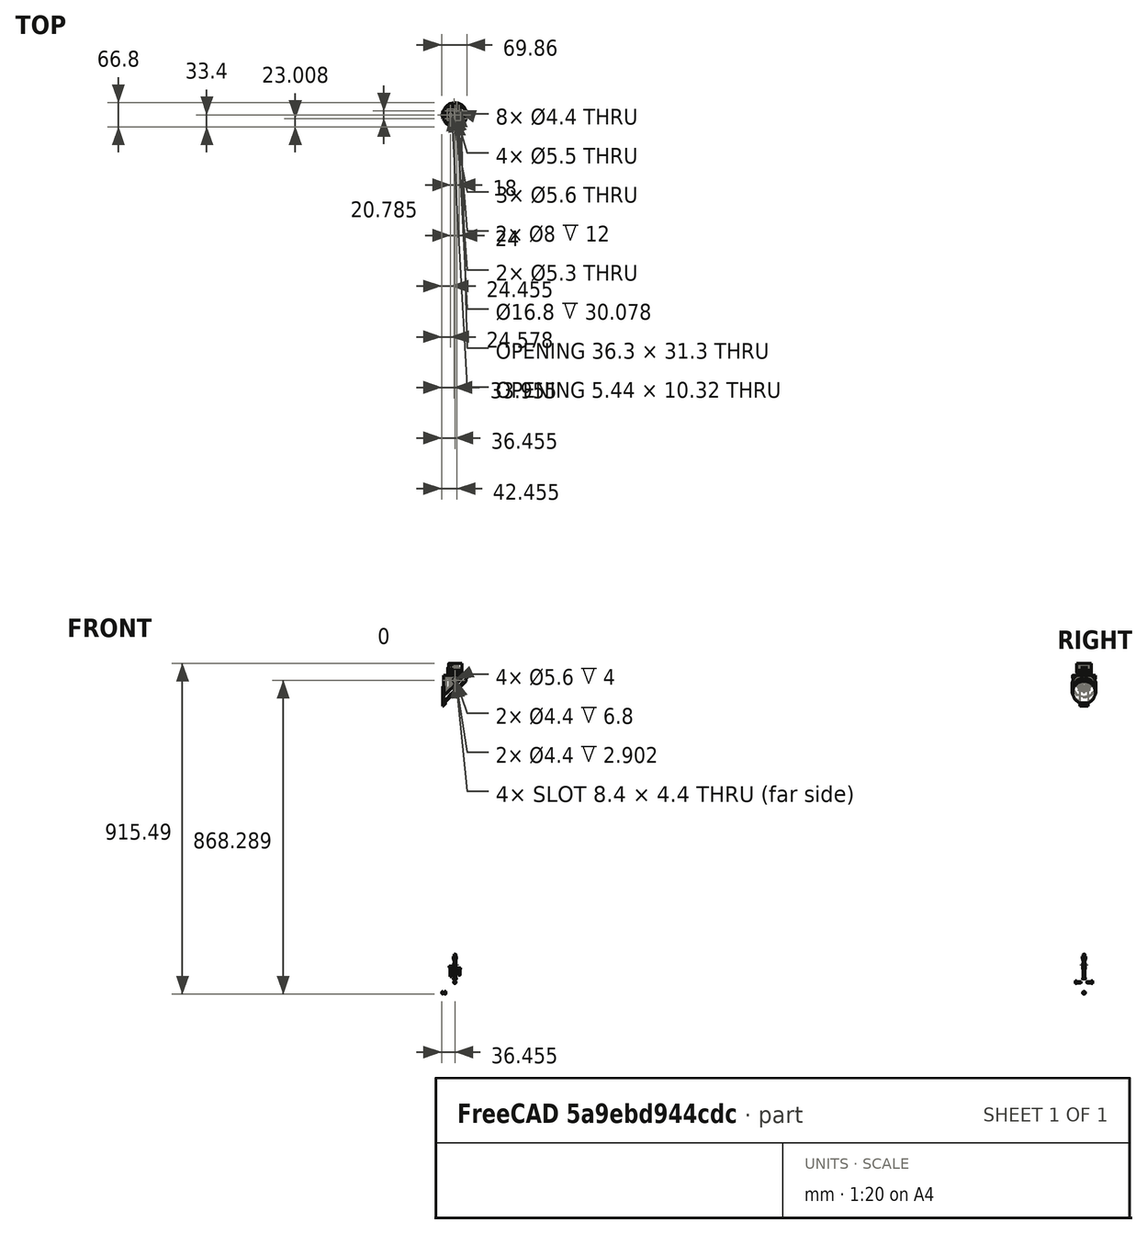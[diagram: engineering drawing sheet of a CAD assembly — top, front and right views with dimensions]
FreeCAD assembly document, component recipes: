
FREECAD ASSEMBLY — COMPONENT RECIPES ("SecondaryMirrorCell")

This assembly document has 9 components, labeled P0..P8 below (a component is one placed body or linked part). 9 of them carry a construction recipe — the FreeCAD feature program that regenerates the part from scratch, quoted from this document or its linked companion documents; the rest are supplied as boundary geometry only. No exploded tour is included for this assembly.
NOTE — this tour is split across 2 documents so each fits a 32k-token context. This is document 1: the component sections continue in the remaining 1 document, each repeating the header above.
COMPONENT P0 — recipe-attached ("MirrorPad", modeled in this document).
Construction recipe (the document's own serialized feature program — sketch geometry with constraints, then the solid features built on it; lengths are millimeters unless a unit is written):

FEATURE [Sketcher::SketchObject] Sketch061  label="MirrorPad_Base_Sketch"
  FullyConstrained = true
  MapMode = 5
  Placement = pos=(0,0,0) rot=(1,0,0;1.5708rad)
  Support = -> [XZ_Plane055]
  expr: Constraints[10] = <<Common>>#<<Parameters>>.sec_padheight
  expr: Constraints[13] = <<Common>>#<<Parameters>>.sec_mtvar
  expr: Constraints[15] = <<Common>>#<<Parameters>>.sec_hubdia / 2
  expr: Constraints[17] = <<Common>>#<<Parameters>>.sec_hubdia * 0.75 / 2
  expr: Constraints[5] = <<Common>>#<<Parameters>>.sec_fillet
  sketch-geometry (6):
    g0: LineSegment StartX=-18 StartY=-14 StartZ=0 EndX=15 EndY=19 EndZ=0
    g1: LineSegment StartX=-20 StartY=30.0779 StartZ=0 EndX=-20 EndY=-14 EndZ=0
    g2: LineSegment StartX=-20 StartY=-14 StartZ=0 EndX=-18 EndY=-14 EndZ=0
    g3: LineSegment StartX=15 StartY=19 StartZ=0 EndX=15 EndY=30.0779 EndZ=0
    g4: LineSegment StartX=15 StartY=30.0779 StartZ=0 EndX=-20 EndY=30.0779 EndZ=0
    g5: GeomPoint X=0 Y=4 Z=0
  constraints (18):
    c: Angle(g-1,g0) = 0.785398
    c: Vertical(g1)
    c: Coincident(g2,g1)
    c: Coincident(g2,g0)
    c: Horizontal(g2)
    c: DistanceX(g2,g2) = 2
    c: Coincident(g3,g0)
    c: Vertical(g3)
    c: Coincident(g4,g3)
    c: Coincident(g1,g4)
    c: DistanceY(g1) = 30.0779
    c: PointOnObject(g5,g0)
    c: PointOnObject(g5,g-2)
    c: DistanceY(g-1,g5) = 4
    c: DistanceY(g3,g3) = 11.0779
    c: DistanceX(g1,g-1) = 20
    c: Horizontal(g4)
    c: DistanceX(g-1,g3) = 15
FEATURE [PartDesign::Pad] Pad  label="MirrorPad_Base"
  Direction = (0,-1,-2e-16)
  Length = 30
  Length2 = 100
  Midplane = true
  Placement = pos=(0,0,0) rot=(1,0,0;1.5708rad)
  Profile = -> Sketch061
  Type = 0
  expr: Length = 2 * ceil(<<Common>>#<<Parameters>>.sec_cpointpos * cos(30)) + <<Common>>#<<Parameters>>.sec_tiltball
FEATURE [PartDesign::Plane] DatumPlane013  label="MirrorPad_DatumPlane_CPoint"
  AttachmentOffset = pos=(0,30.0779,-12) rot=(0,0,1;0rad)
  Length = 60.4955
  MapMode = 5
  Placement = pos=(-12,9.3e-15,30.0779) rot=(0.57735,0.57735,0.57735;2.0944rad)
  ResizeMode = 0
  Support = -> [YZ_Plane055]
  Width = 65.5734
  expr: .AttachmentOffset.Base.y = <<Common>>#<<Parameters>>.sec_padheight
  expr: .AttachmentOffset.Base.z = -<<Common>>#<<Parameters>>.sec_cpointpos
FEATURE [Sketcher::SketchObject] Sketch002  label="MirrorPad_CollGroove_Sketch"
  FullyConstrained = true
  MapMode = 5
  Placement = pos=(-12,9.3e-15,30.0779) rot=(0.57735,0.57735,0.57735;2.0944rad)
  Support = -> [DatumPlane013]
  expr: Constraints[12] = <<Common>>#<<Parameters>>.sec_tiltball / 2
  expr: Constraints[4] = ceil(<<Common>>#<<Parameters>>.sec_tiltball * sqrt(2) / 2) + 1
  sketch-geometry (5):
    g0: LineSegment StartX=-3.5 StartY=0 StartZ=0 EndX=0 EndY=-2.02073 EndZ=0
    g1: LineSegment StartX=0 StartY=-2.02073 StartZ=0 EndX=3.5 EndY=0 EndZ=0
    g2: LineSegment StartX=-3.5 StartY=0 StartZ=0 EndX=-3.5 EndY=4 EndZ=0
    g3: LineSegment StartX=-3.5 StartY=4 StartZ=0 EndX=3.5 EndY=4 EndZ=0
    g4: LineSegment StartX=3.5 StartY=4 StartZ=0 EndX=3.5 EndY=0 EndZ=0
  constraints (14):
    c: PointOnObject(g0,g-1)
    c: Symmetric(g0,g1,g-2)
    c: PointOnObject(g0,g-2)
    c: Coincident(g1,g0)
    c: DistanceX(g0,g1) = 7
    c: Coincident(g2,g0)
    c: Vertical(g2)
    c: Coincident(g3,g2)
    c: Horizontal(g3)
    c: Coincident(g4,g3)
    c: Coincident(g4,g1)
    c: Vertical(g4)
    c: DistanceY(g4,g4) = 4
    c: Angle(g-1,g1) = 0.523599
FEATURE [PartDesign::Plane] DatumPlane001  label="MirrorPad_DatumPlane_Top"
  AttachmentOffset = pos=(0,0,30.0779) rot=(0,0,1;0rad)
  Length = 60
  MapMode = 5
  Placement = pos=(0,0,30.0779) rot=(0,0,1;0rad)
  ResizeMode = 0
  Support = -> [XY_Plane055]
  Width = 60
  expr: .AttachmentOffset.Base.z = <<Common>>#<<Parameters>>.sec_padheight
FEATURE [Sketcher::SketchObject] Sketch005  label="MirrorPad_Outer_Sketch"
  FullyConstrained = true
  MapMode = 5
  Support = -> [XY_Plane055]
  expr: Constraints[2] = <<Common>>#<<Parameters>>.sec_hubdia
  expr: Constraints[3] = <<Common>>#<<Parameters>>.sec_mdia * 2
  sketch-geometry (2):
    g0: Circle CenterX=0 CenterY=0 CenterZ=0 NormalX=0 NormalY=0 NormalZ=1 AngleXU=0 Radius=20
    g1: Circle CenterX=0 CenterY=0 CenterZ=0 NormalX=0 NormalY=0 NormalZ=1 AngleXU=0 Radius=62.5
  constraints (4):
    c: Coincident(g0,g-1)
    c: Coincident(g1,g0)
    c: Diameter(g0) = 40
    c: Diameter(g1) = 125
FEATURE [PartDesign::CoordinateSystem] Local_CS003  label="LCS_TiltPlateAttachment"
  AttacherType = Attacher::AttachEngine3D
  AttachmentOffset = pos=(0,0,33.201) rot=(0,0,1;0rad)
  MapMode = 5
  Placement = pos=(0,0,33.201) rot=(0,0,1;0rad)
  Support = -> [XY_Plane055]
  expr: .AttachmentOffset.Base.z = <<Common>>#<<Parameters>>.sec_padheight + <<Common>>#<<Parameters>>.sec_tiltspacing
FEATURE [PartDesign::CoordinateSystem] Local_CS053  label="LCS_SecondaryPad"
  AttacherType = Attacher::AttachEngine3D
  MapMode = 5
  Support = -> [XY_Plane055]
FEATURE [PartDesign::Plane] DatumPlane031  label="MirrorPad_DatumPlane_Cavity"
  AttachmentOffset = pos=(0,0,-4) rot=(0,0,1;0rad)
  Length = 60
  MapMode = 2
  Placement = pos=(0,0,26.0779) rot=(0,0,1;0rad)
  ResizeMode = 0
  Support = -> [DatumPlane001]
  Width = 60
  expr: .AttachmentOffset.Base.z = -<<Common>>#<<Parameters>>.sec_pthick / 2
FEATURE [Sketcher::SketchObject] Sketch001  label="MirrorPad_Cavity_Sketch"
  FullyConstrained = true
  MapMode = 5
  Placement = pos=(0,0,26.0779) rot=(0,0,1;0rad)
  Support = -> [DatumPlane031]
  sketch-geometry (5):
    g0: LineSegment StartX=-4.2 StartY=4.2 StartZ=0 EndX=4.2 EndY=4.2 EndZ=0
    g1: LineSegment StartX=-4.2 StartY=-4.2 StartZ=0 EndX=4.2 EndY=-4.2 EndZ=0
    g2: ArcOfCircle CenterX=4.2 CenterY=0 CenterZ=0 NormalX=0 NormalY=0 NormalZ=1 AngleXU=0 Radius=4.2 StartAngle=4.71239 EndAngle=7.85398
    g3: ArcOfCircle CenterX=-4.2 CenterY=0 CenterZ=0 NormalX=0 NormalY=0 NormalZ=1 AngleXU=0 Radius=4.2 StartAngle=1.5708 EndAngle=4.71239
    g4: LineSegment StartX=-4.2 StartY=4.2 StartZ=0 EndX=-4.2 EndY=-4.2 EndZ=0
  constraints (15):
    c: Horizontal(g1)
    c: Equal(g1,g0)
    c: Coincident(g2,g0)
    c: Coincident(g2,g1)
    c: Coincident(g3,g0)
    c: Coincident(g3,g1)
    c: DistanceY(g1,g0) = 8.4
    c: Symmetric(g0,g0,g-2)
    c: Diameter(g2) = 8.4
    c: Equal(g2,g3)
    c: DistanceX(g0,g0) = 8.4
    c: PointOnObject(g2,g-1)
    c: Coincident(g4,g0)
    c: Coincident(g4,g1)
    c: Vertical(g4)
FEATURE [Sketcher::SketchObject] Sketch062  label="MirrorPad_CHole_Sketch"
  FullyConstrained = true
  MapMode = 5
  Placement = pos=(0,0,26.0779) rot=(0,0,1;0rad)
  Support = -> [DatumPlane031]
  expr: Constraints[6] = <<Common>>#<<Parameters>>.sec_centralbolt * 1.2
  expr: Constraints[7] = <<Common>>#<<Parameters>>.sec_centralbolt / 2
  sketch-geometry (4):
    g0: ArcOfCircle CenterX=-1.25 CenterY=0 CenterZ=0 NormalX=0 NormalY=0 NormalZ=1 AngleXU=0 Radius=3 StartAngle=1.5708 EndAngle=4.71239
    g1: ArcOfCircle CenterX=1.25 CenterY=0 CenterZ=0 NormalX=0 NormalY=0 NormalZ=1 AngleXU=0 Radius=3 StartAngle=4.71239 EndAngle=7.85398
    g2: LineSegment StartX=-1.25 StartY=-3 StartZ=0 EndX=1.25 EndY=-3 EndZ=0
    g3: LineSegment StartX=-1.25 StartY=3 StartZ=0 EndX=1.25 EndY=3 EndZ=0
  constraints (9):
    c: Tangent(g0,g3) = 1.5708
    c: Tangent(g0,g2) = -1.5708
    c: Tangent(g2,g1) = -1.5708
    c: Tangent(g3,g1) = 1.5708
    c: Horizontal(g2)
    c: PointOnObject(g0,g-1)
    c: Diameter(g0) = 6
    c: DistanceX(g3,g3) = 2.5
    c: Symmetric(g0,g1,g-2)
FEATURE [PartDesign::CoordinateSystem] Local_CS123  label="LCS_HubPoint"
  AttacherType = Attacher::AttachEngine3D
  MapMode = 5
  Placement = pos=(0,0,26.0779) rot=(0,0,1;0rad)
  Support = -> [DatumPlane031]
  expr: .AttachmentOffset.Base.z = 0
FEATURE [PartDesign::Pocket] Pocket049  label="MirrorPad_Cavity"
  BaseFeature = -> Pad
  Direction = (0,0,-1)
  Length = 5
  Length2 = 100
  Placement = pos=(0,0,0) rot=(1,0,0;1.5708rad)
  Profile = -> Sketch001
  Type = 1
FEATURE [PartDesign::Pocket] Pocket050  label="MirrorPad_CentralHole"
  BaseFeature = -> Pocket049
  Direction = (0,0,-1)
  Length = 5
  Length2 = 100
  Placement = pos=(0,0,0) rot=(1,0,0;1.5708rad)
  Profile = -> Sketch062
  Reversed = true
  Type = 1
FEATURE [PartDesign::Pocket] Pocket060  label="MirrorPad_Outer"
  BaseFeature = -> Pocket050
  Direction = (0,0,-1)
  Length = 5
  Length2 = 100
  Midplane = true
  Placement = pos=(0,0,0) rot=(1,0,0;1.5708rad)
  Profile = -> Sketch005
  Type = 1
FEATURE [PartDesign::Pocket] Pocket065  label="MirrorPad_CollGroove"
  BaseFeature = -> Pocket060
  Direction = (-1,1e-16,-1e-16)
  Length = 8
  Length2 = 6
  Midplane = true
  Placement = pos=(0,0,0) rot=(1,0,0;1.5708rad)
  Profile = -> Sketch002
  Type = 4
  expr: Length = <<Common>>#<<Parameters>>.sec_hubdia / 2 - <<Common>>#<<Parameters>>.sec_cpointpos
  expr: Length2 = <<Common>>#<<Parameters>>.sec_tiltball * 1.5 / 2
FEATURE [PartDesign::PolarPattern] PolarPattern  label="MirrorPad_CollGroove_Polar"
  Angle = 360
  Axis = -> Z_Axis055
  BaseFeature = -> Pocket065
  Occurrences = 3
  Originals = -> [Pocket065]
  Placement = pos=(0,0,0) rot=(1,0,0;1.5708rad)
FEATURE [Sketcher::SketchObject] Sketch126  label="MirrorPad_InnerShaft_Sketch"
  FullyConstrained = true
  MapMode = 5
  Placement = pos=(0,0,0) rot=(1,0,0;1.5708rad)
  Support = -> [XZ_Plane055]
  expr: Constraints[1] = <<Common>>#<<Parameters>>.sec_collbolt * 1.1
  expr: Constraints[2] = <<Common>>#<<Parameters>>.sec_mtvar + <<Common>>#<<Parameters>>.sec_hubdia / 4
  sketch-geometry (1):
    g0: Circle CenterX=0 CenterY=14 CenterZ=0 NormalX=0 NormalY=0 NormalZ=1 AngleXU=0 Radius=2.2
  constraints (3):
    c: PointOnObject(g0,g-2)
    c: Diameter(g0) = 4.4
    c: DistanceY(g0) = 14
FEATURE [Sketcher::SketchObject] Sketch125  label="MirrorPad_InnerNut_Sketch"
  AttachmentOffset = pos=(0,0,15) rot=(0,0,1;0rad)
  ExternalGeometry = -> [Sketch126]
  FullyConstrained = true
  MapMode = 5
  Placement = pos=(0,-15,-3.3e-15) rot=(1,0,0;1.5708rad)
  Support = -> [XZ_Plane055]
  expr: .AttachmentOffset.Base.z = (2 * ceil(<<Common>>#<<Parameters>>.sec_cpointpos * cos(30)) + <<Common>>#<<Parameters>>.sec_tiltball) / 2
  expr: Constraints[1] = <<Common>>#<<Parameters>>.acc_M4Bore
  sketch-geometry (1):
    g0: Circle CenterX=0 CenterY=14 CenterZ=0 NormalX=0 NormalY=0 NormalZ=1 AngleXU=0 Radius=2.8
  constraints (2):
    c: Coincident(g0,g-3)
    c: Diameter(g0) = 5.6
FEATURE [PartDesign::Pocket] Pocket066  label="MirrorPad_InnerShaft"
  BaseFeature = -> PolarPattern
  Direction = (0,1,2e-16)
  Length = 5
  Length2 = 100
  Midplane = true
  Placement = pos=(0,0,0) rot=(1,0,0;1.5708rad)
  Profile = -> Sketch126
  Type = 1
FEATURE [Sketcher::SketchObject] Sketch138  label="MirrorPad_InnerCut_Sketch"
  FullyConstrained = true
  MapMode = 5
  Placement = pos=(0,0,0) rot=(1,0,0;1.5708rad)
  Support = -> [XZ_Plane055]
  expr: Constraints[10] = -<<Common>>#<<Parameters>>.sec_mdia / 2
  expr: Constraints[11] = <<Common>>#<<Parameters>>.sec_hubdia / 8 + 1
  expr: Constraints[8] = -<<Common>>#<<Parameters>>.sec_hubdia * 0.75 / 2
  expr: Constraints[9] = <<Common>>#<<Parameters>>.sec_padheight - <<Common>>#<<Parameters>>.sec_pthick
  sketch-geometry (4):
    g0: LineSegment StartX=-21 StartY=22.0779 StartZ=0 EndX=-15 EndY=22.0779 EndZ=0
    g1: LineSegment StartX=-15 StartY=22.0779 StartZ=0 EndX=-15 EndY=-31.25 EndZ=0
    g2: LineSegment StartX=-15 StartY=-31.25 StartZ=0 EndX=-21 EndY=-31.25 EndZ=0
    g3: LineSegment StartX=-21 StartY=-31.25 StartZ=0 EndX=-21 EndY=22.0779 EndZ=0
  constraints (12):
    c: Coincident(g0,g1)
    c: Coincident(g1,g2)
    c: Coincident(g2,g3)
    c: Coincident(g3,g0)
    c: Horizontal(g0)
    c: Horizontal(g2)
    c: Vertical(g1)
    c: Vertical(g3)
    c: DistanceX(g0) = -15
    c: DistanceY(g0) = 22.0779
    c: DistanceY(g1) = -31.25
    c: DistanceX(g0,g0) = 6
FEATURE [PartDesign::CoordinateSystem] Local_CS227  label="LCS_Top"
  AttacherType = Attacher::AttachEngine3D
  MapMode = 5
  Placement = pos=(0,0,30.0779) rot=(0,0,1;0rad)
  Support = -> [DatumPlane001]
FEATURE [PartDesign::Pocket] Pocket190  label="MirrorPad_InnerCut"
  BaseFeature = -> Pocket066
  Direction = (0,1,2e-16)
  Length = 5
  Length2 = 100
  Midplane = true
  Placement = pos=(0,0,0) rot=(1,0,0;1.5708rad)
  Profile = -> Sketch138
  Type = 1
FEATURE [PartDesign::Pocket] Pocket191  label="MirrorPad_InnerNut"
  BaseFeature = -> Pocket190
  Direction = (0,1,2e-16)
  Length = 4
  Length2 = 100
  Placement = pos=(0,0,0) rot=(1,0,0;1.5708rad)
  Profile = -> Sketch125
  Type = 0
FEATURE [PartDesign::Mirrored] Mirrored008  label="MirrorPad_InnerNut_Mirror"
  BaseFeature = -> Pocket191
  MirrorPlane = -> XZ_Plane055
  Originals = -> [Pocket191]
  Placement = pos=(0,0,0) rot=(1,0,0;1.5708rad)
FEATURE [PartDesign::CoordinateSystem] Local_CS224  label="LCS_SideNut_F"
  AttacherType = Attacher::AttachEngine3D
  MapMode = 11
  Placement = pos=(0,-15,14) rot=(0.57735,-0.57735,-0.57735;4.18879rad)
  Support = -> [Mirrored008]
FEATURE [PartDesign::CoordinateSystem] Local_CS225  label="LCS_SideNut_A"
  AttacherType = Attacher::AttachEngine3D
  MapMode = 11
  Placement = pos=(0,15,14) rot=(0.57735,-0.57735,0.57735;2.0944rad)
  Support = -> [Mirrored008]
FEATURE [PartDesign::Chamfer] Chamfer002  label="MirrorPad_Chamfer"
  Angle = 45
  Base = -> Mirrored008 [Edge4,Edge5,Edge6,Edge7,Edge8,Edge1,Edge9,Edge10,Edge11,Edge12,Edge3,Edge2,Edge36,Edge41]
  BaseFeature = -> Mirrored008
  ChamferType = 0
  FlipDirection = false
  Placement = pos=(0,0,0) rot=(1,0,0;1.5708rad)
  Size = 0.6
  Size2 = 0.4
  SupportTransform = false
  UseAllEdges = false
FEATURE [PartDesign::Body] Body001  label="MirrorPad"
  Group = -> [Sketch061,Pad,Sketch001,DatumPlane013,Sketch002,Sketch062,DatumPlane001,Sketch005,Local_CS123,Local_CS003,Local_CS053,DatumPlane031,Pocket049,Pocket050,Pocket060,Pocket065,PolarPattern,Sketch125,Sketch126,Pocket066,Sketch138,Local_CS224,Local_CS225,Local_CS227,Pocket190,Pocket191,Mirrored008,Chamfer002]
  Origin = -> Origin055
  Placement = pos=(-3.125,0,854.799) rot=(0,0,1;0rad)
  Tip = -> Chamfer002
  expr: .Placement.Base.x = -<<Common>>#<<Parameters>>.sec_offset_x
  expr: .Placement.Base.z = <<Common>>#<<Parameters>>.datum_sec_mirrorpad
COMPONENT P1 — recipe-attached ("SpiderHub_Main", modeled in this document).
Construction recipe (the document's own serialized feature program — sketch geometry with constraints, then the solid features built on it; lengths are millimeters unless a unit is written):

FEATURE [PartDesign::CoordinateSystem] Local_CS055  label="LCS_Hub_Upper"
  AttacherType = Attacher::AttachEngine3D
  AttachmentOffset = pos=(0,0,20) rot=(0,0,1;1.5708rad)
  MapMode = 5
  Placement = pos=(0,0,20) rot=(0,0,1;1.5708rad)
  Support = -> [XY_Plane058]
  expr: .AttachmentOffset.Base.z = <<Common>>#<<Parameters>>.sec_stalkheight
FEATURE [PartDesign::CoordinateSystem] Local_CS136  label="LCS_BoltZrot"
  AttacherType = Attacher::AttachEngine3D
  AttachmentOffset = pos=(12,0,8) rot=(0,0,1;0rad)
  MapMode = 5
  Placement = pos=(12,0,8) rot=(0,0,1;0rad)
  Support = -> [XY_Plane058]
  expr: .AttachmentOffset.Base.x = <<Common>>#<<Parameters>>.sec_cpointpos
  expr: .AttachmentOffset.Base.z = <<Common>>#<<Parameters>>.sec_pthick
FEATURE [PartDesign::CoordinateSystem] Local_CS060  label="LCS_BoltTilt"
  AttacherType = Attacher::AttachEngine3D
  AttachmentOffset = pos=(-12,0,8) rot=(0,0,1;0rad)
  MapMode = 5
  Placement = pos=(-12,0,8) rot=(0,0,1;0rad)
  Support = -> [XY_Plane058]
  expr: .AttachmentOffset.Base.x = -<<Common>>#<<Parameters>>.sec_cpointpos
  expr: .AttachmentOffset.Base.z = <<Common>>#<<Parameters>>.sec_pthick
FEATURE [PartDesign::CoordinateSystem] Local_CS062  label="LCS_HubLower"
  AttacherType = Attacher::AttachEngine3D
  MapMode = 5
  Support = -> [XY_Plane058]
FEATURE [PartDesign::Plane] DatumPlane019  label="UpperHub_DatumPlane_Top"
  AttachmentOffset = pos=(0,0,20) rot=(0,0,1;0rad)
  Length = 60
  MapMode = 5
  Placement = pos=(0,0,20) rot=(0,0,1;0rad)
  ResizeMode = 0
  Support = -> [XY_Plane058]
  Width = 60
  expr: .AttachmentOffset.Base.z = <<Common>>#<<Parameters>>.sec_stalkheight
FEATURE [Sketcher::SketchObject] Sketch112  label="UpperHub_MasterSketch"
  FullyConstrained = true
  MapMode = 5
  Support = -> [XY_Plane058]
  expr: Constraints[1] = <<Common>>#<<Parameters>>.pri_poledia + <<Common>>#<<Parameters>>.sec_fthick * 2
  expr: Constraints[21] = <<Common>>#<<Parameters>>.sec_sidebolt * 1.5
  expr: Constraints[23] = <<Common>>#<<Parameters>>.sec_hubdia
  expr: Constraints[26] = <<Common>>#<<Parameters>>.sec_poledia + <<Common>>#<<Parameters>>.sec_clamptol
  expr: Constraints[29] = <<Common>>#<<Parameters>>.sec_collbolt
  expr: Constraints[32] = <<Common>>#<<Parameters>>.sec_cpointpos
  expr: Constraints[33] = <<Common>>#<<Parameters>>.sec_poledia / 2 - <<Common>>#<<Parameters>>.sec_spthick
  expr: Constraints[35] = <<Common>>#<<Parameters>>.bolt_y - <<Common>>#<<Parameters>>.pri_poledia / 2
  expr: Constraints[3] = <<Common>>#<<Parameters>>.bolt_x + <<Common>>#<<Parameters>>.sec_offset_x
  expr: Constraints[4] = <<Common>>#<<Parameters>>.bolt_y
  expr: Constraints[61] = -<<Common>>#<<Parameters>>.bolt_x + <<Common>>#<<Parameters>>.sec_offset_x
  expr: Constraints[64] = <<Common>>#<<Parameters>>.sec_intloop
  expr: Constraints[65] = <<Common>>#<<Parameters>>.sec_offset_x
  expr: Constraints[70] = <<Common>>#<<Parameters>>.sec_toparc_angle
  expr: Constraints[79] = <<Common>>#<<Parameters>>.sec_zrotmax
  expr: Constraints[87] = <<Common>>#<<Parameters>>.sec_collbolt
  expr: Constraints[88] = <<Common>>#<<Parameters>>.sec_fillet
  sketch-geometry (34):
    g0: Circle CenterX=116.125 CenterY=113 CenterZ=0 NormalX=0 NormalY=0 NormalZ=1 AngleXU=0 Radius=13
    g1: Circle CenterX=116.125 CenterY=-113 CenterZ=0 NormalX=0 NormalY=0 NormalZ=1 AngleXU=0 Radius=13
    g2: LineSegment StartX=-23.7451 StartY=0 StartZ=0 EndX=102.255 EndY=126 EndZ=0
    g3: LineSegment StartX=-23.7451 StartY=0 StartZ=0 EndX=102.255 EndY=-126 EndZ=0
    g4: LineSegment StartX=116.125 StartY=126 StartZ=0 EndX=102.255 EndY=126 EndZ=0
    g5: LineSegment StartX=116.125 StartY=-126 StartZ=0 EndX=102.255 EndY=-126 EndZ=0
    g6: LineSegment StartX=102.69 StartY=126.435 StartZ=0 EndX=116.125 EndY=113 EndZ=0
    g7: GeomPoint X=106.933 Y=122.192 Z=0
    g8: Circle CenterX=0 CenterY=0 CenterZ=0 NormalX=0 NormalY=0 NormalZ=1 AngleXU=0 Radius=20
    g9: Circle CenterX=116.125 CenterY=113 CenterZ=0 NormalX=0 NormalY=0 NormalZ=1 AngleXU=0 Radius=9.35
    g10: Circle CenterX=116.125 CenterY=-113 CenterZ=0 NormalX=0 NormalY=0 NormalZ=1 AngleXU=0 Radius=9.35
    g11: Circle CenterX=-12 CenterY=0 CenterZ=0 NormalX=0 NormalY=0 NormalZ=1 AngleXU=0 Radius=2
    g12: Circle CenterX=12 CenterY=0 CenterZ=0 NormalX=0 NormalY=0 NormalZ=1 AngleXU=0 Radius=2
    g13: LineSegment StartX=124.125 StartY=103 StartZ=0 EndX=124.125 EndY=-103 EndZ=0
    g14: LineSegment StartX=103.125 StartY=113 StartZ=0 EndX=129.125 EndY=113 EndZ=0
    g15: LineSegment StartX=103.125 StartY=-113 StartZ=0 EndX=129.125 EndY=-113 EndZ=0
    g16: LineSegment StartX=103.125 StartY=113 StartZ=0 EndX=103.125 EndY=-113 EndZ=0
    g17: LineSegment StartX=129.125 StartY=-113 StartZ=0 EndX=129.125 EndY=113 EndZ=0
    g18: LineSegment StartX=-4.18858 StartY=19.5565 StartZ=0 EndX=-4.18858 EndY=-19.5565 EndZ=0
    g19: GeomPoint X=116.125 Y=139.87 Z=0
    g20: LineSegment StartX=116.125 StartY=113 StartZ=0 EndX=116.125 EndY=139.87 EndZ=0
    g21: Circle CenterX=-109.875 CenterY=0 CenterZ=0 NormalX=0 NormalY=0 NormalZ=1 AngleXU=0 Radius=9.35
    g22: Circle CenterX=-109.875 CenterY=0 CenterZ=0 NormalX=0 NormalY=0 NormalZ=1 AngleXU=0 Radius=13
    g23: Circle CenterX=3.125 CenterY=-3.4e-15 CenterZ=0 NormalX=0 NormalY=0 NormalZ=1 AngleXU=0 Radius=115
    g24: LineSegment StartX=3.125 StartY=-3.4e-15 StartZ=0 EndX=-62.8363 EndY=94.2025 EndZ=0
    g25: LineSegment StartX=3.125 StartY=-3.4e-15 StartZ=0 EndX=-62.8363 EndY=-94.2025 EndZ=0
    g26: ArcOfCircle CenterX=0 CenterY=0 CenterZ=0 NormalX=0 NormalY=0 NormalZ=1 AngleXU=0 Radius=8.05894 StartAngle=2.92343 EndAngle=3.35976
    g27: ArcOfCircle CenterX=3.125 CenterY=-3.4e-15 CenterZ=0 NormalX=0 NormalY=0 NormalZ=1 AngleXU=0 Radius=15.125 StartAngle=2.96816 EndAngle=3.31502
    g28: LineSegment StartX=-11.7731 StartY=2.61003 StartZ=0 EndX=0 EndY=0 EndZ=0
    g29: LineSegment StartX=-11.7731 StartY=-2.61003 StartZ=0 EndX=0 EndY=0 EndZ=0
    g30: ArcOfCircle CenterX=-11.7731 CenterY=2.61003 CenterZ=0 NormalX=0 NormalY=0 NormalZ=1 AngleXU=0 Radius=4 StartAngle=6.06502 EndAngle=7.94739
    g31: ArcOfCircle CenterX=-11.7731 CenterY=-2.61003 CenterZ=0 NormalX=0 NormalY=0 NormalZ=1 AngleXU=0 Radius=4 StartAngle=4.61898 EndAngle=6.50135
    g32: ArcOfCircle CenterX=-12.3328 CenterY=8.58387 CenterZ=0 NormalX=0 NormalY=0 NormalZ=1 AngleXU=0 Radius=2 StartAngle=2.35619 EndAngle=4.8058
    g33: ArcOfCircle CenterX=-12.3328 CenterY=-8.58387 CenterZ=0 NormalX=0 NormalY=0 NormalZ=1 AngleXU=0 Radius=2 StartAngle=1.47738 EndAngle=3.92699
  constraints (94):
    c: Equal(g1,g0)
    c: Diameter(g0) = 26
    c: Symmetric(g1,g0,g-1)
    c: DistanceX(g0) = 116.125
    c: DistanceY(g0) = 113
    c: PointOnObject(g2,g-1)
    c: Coincident(g3,g2)
    c: Perpendicular(g3,g2)
    c: PointOnObject(g4,g0)
    c: Coincident(g4,g2)
    c: Horizontal(g4)
    c: Tangent(g4,g0)
    c: PointOnObject(g5,g1)
    c: Horizontal(g5)
    c: Coincident(g5,g3)
    c: Symmetric(g3,g2,g-1)
    c: PointOnObject(g6,g2)
    c: Coincident(g6,g0)
    c: Perpendicular(g2,g6)
    c: PointOnObject(g7,g6)
    c: PointOnObject(g7,g0)
    c: Distance(g7,g6) = 6
    c: Coincident(g8,g-1)
    c: Diameter(g8) = 40
    c: Coincident(g9,g0)
    c: Coincident(g10,g1)
    c: Diameter(g10) = 18.7
    c: Equal(g10,g9)
    c: PointOnObject(g11,g-1)
    c: Diameter(g11) = 4
    c: Equal(g11,g12)
    c: Symmetric(g11,g12,g-2)
    c: DistanceX(g12) = 12
    c: DistanceX(g6,g13) = 8
    c: Symmetric(g13,g13,g-1)
    c: DistanceY(g13) = 103
    c: PointOnObject(g14,g0)
    c: PointOnObject(g14,g0)
    c: Horizontal(g14)
    c: PointOnObject(g15,g1)
    c: Horizontal(g15)
    c: PointOnObject(g1,g15)
    c: PointOnObject(g6,g14)
    c: Coincident(g16,g14)
    c: Coincident(g16,g15)
    c: Vertical(g16)
    c: Coincident(g17,g15)
    c: Coincident(g17,g14)
    c: PointOnObject(g18,g2)
    c: PointOnObject(g18,g3)
    c: Vertical(g18)
    c: PointOnObject(g18,g8)
    c: Distance(g2,g6) = 0.615224
    c: DistanceX(g2) = -23.7451
    c: PointOnObject(g19,g2)
    c: Coincident(g20,g0)
    c: Coincident(g20,g19)
    c: Vertical(g20)
    c: DistanceY(g19) = 139.87
    c: PointOnObject(g21,g-1)
    c: Coincident(g22,g21)
    c: DistanceX(g21) = -109.875
    c: Equal(g21,g10)
    c: Equal(g22,g1)
    c: Radius(g23) = 115
    c: DistanceX(g-1,g23) = 3.125
    c: Coincident(g24,g23)
    c: PointOnObject(g24,g23)
    c: Coincident(g25,g23)
    c: Symmetric(g24,g25,g-1)
    c: Angle(g24,g-1) = 0.959931
    c: DistanceY(g4) = 126
    c: Coincident(g26,g8)
    c: Coincident(g27,g23)
    c: Coincident(g28,g27)
    c: Coincident(g28,g8)
    c: Coincident(g29,g27)
    c: Coincident(g29,g8)
    c: Symmetric(g27,g27,g-1)
    c: Angle(g28,g29) = 0.436332
    c: Coincident(g30,g26)
    c: Coincident(g31,g27)
    c: Coincident(g31,g26)
    c: PointOnObject(g26,g28)
    c: PointOnObject(g26,g29)
    c: Coincident(g30,g27)
    c: PointOnObject(g11,g27)
    c: Radius(g30) = 4
    c: Radius(g32) = 2
    c: Tangent(g33,g3) = -1.5708
    c: Tangent(g33,g31) = 1.5708
    c: Tangent(g32,g2) = 1.5708
    c: Tangent(g32,g30) = 1.5708
    c: Equal(g33,g32)
FEATURE [Sketcher::SketchObject] Sketch118  label="UpperHub_Main_LowerNut_Sketch"
  FullyConstrained = true
  MapMode = 5
  Support = -> [XY_Plane058]
  expr: Constraints[61] = <<Common>>#<<Parameters>>.sec_cpointpos
  sketch-geometry (25):
    g0: LineSegment StartX=-9.92154 StartY=-3.6 StartZ=0 EndX=-7.84308 EndY=8.13e-14 EndZ=0
    g1: LineSegment StartX=-7.84308 StartY=8.13e-14 StartZ=0 EndX=-9.92154 EndY=3.6 EndZ=0
    g2: LineSegment StartX=-9.92154 StartY=3.6 StartZ=0 EndX=-14.0785 EndY=3.6 EndZ=0
    g3: LineSegment StartX=-14.0785 StartY=3.6 StartZ=0 EndX=-16.1569 EndY=-8.17e-14 EndZ=0
    g4: LineSegment StartX=-16.1569 StartY=-8.17e-14 StartZ=0 EndX=-14.0785 EndY=-3.6 EndZ=0
    g5: LineSegment StartX=-14.0785 StartY=-3.6 StartZ=0 EndX=-9.92154 EndY=-3.6 EndZ=0
    g6: Circle CenterX=-12 CenterY=0 CenterZ=0 NormalX=0 NormalY=0 NormalZ=1 AngleXU=0 Radius=4.15692
    g7: LineSegment StartX=8.07846 StartY=6.7923 StartZ=0 EndX=10.1569 EndY=10.3923 EndZ=0
    g8: LineSegment StartX=10.1569 StartY=10.3923 StartZ=0 EndX=8.07846 EndY=13.9923 EndZ=0
    g9: LineSegment StartX=8.07846 StartY=13.9923 StartZ=0 EndX=3.92154 EndY=13.9923 EndZ=0
    g10: LineSegment StartX=3.92154 StartY=13.9923 StartZ=0 EndX=1.84308 EndY=10.3923 EndZ=0
    g11: LineSegment StartX=1.84308 StartY=10.3923 StartZ=0 EndX=3.92154 EndY=6.7923 EndZ=0
    g12: LineSegment StartX=3.92154 StartY=6.7923 StartZ=0 EndX=8.07846 EndY=6.7923 EndZ=0
    g13: Circle CenterX=6 CenterY=10.3923 CenterZ=0 NormalX=0 NormalY=0 NormalZ=1 AngleXU=0 Radius=4.15692
    g14: LineSegment StartX=8.07846 StartY=-13.9923 StartZ=0 EndX=10.1569 EndY=-10.3923 EndZ=0
    g15: LineSegment StartX=10.1569 StartY=-10.3923 StartZ=0 EndX=8.07846 EndY=-6.7923 EndZ=0
    g16: LineSegment StartX=8.07846 StartY=-6.7923 StartZ=0 EndX=3.92154 EndY=-6.7923 EndZ=0
    g17: LineSegment StartX=3.92154 StartY=-6.7923 StartZ=0 EndX=1.84308 EndY=-10.3923 EndZ=0
    g18: LineSegment StartX=1.84308 StartY=-10.3923 StartZ=0 EndX=3.92154 EndY=-13.9923 EndZ=0
    g19: LineSegment StartX=3.92154 StartY=-13.9923 StartZ=0 EndX=8.07846 EndY=-13.9923 EndZ=0
    g20: Circle CenterX=6 CenterY=-10.3923 CenterZ=0 NormalX=0 NormalY=0 NormalZ=1 AngleXU=0 Radius=4.15692
    g21: LineSegment StartX=-12 StartY=0 StartZ=0 EndX=6 EndY=10.3923 EndZ=0
    g22: LineSegment StartX=6 StartY=10.3923 StartZ=0 EndX=6 EndY=-10.3923 EndZ=0
    g23: LineSegment StartX=6 StartY=-10.3923 StartZ=0 EndX=-12 EndY=0 EndZ=0
    g24: Circle CenterX=0 CenterY=0 CenterZ=0 NormalX=0 NormalY=0 NormalZ=1 AngleXU=0 Radius=12
  constraints (59):
    c: Coincident(g0,g1)
    c: Coincident(g1,g2)
    c: Coincident(g2,g3)
    c: Coincident(g3,g4)
    c: Coincident(g4,g5)
    c: Coincident(g5,g0)
    c: Equal(g0, g1-g5) x5
    c: PointOnObject(g0,g6)
    c: PointOnObject(g1,g6)
    c: PointOnObject(g2,g6)
    c: PointOnObject(g3,g6)
    c: PointOnObject(g4,g6)
    c: PointOnObject(g5,g6)
    c: PointOnObject(g6,g-1)
    c: Coincident(g7,g8)
    c: Coincident(g8,g9)
    c: Coincident(g9,g10)
    c: Coincident(g10,g11)
    c: Coincident(g11,g12)
    c: Coincident(g12,g7)
    c: Equal(g7, g8-g12) x5
    c: PointOnObject(g7,g13)
    c: PointOnObject(g8,g13)
    c: PointOnObject(g9,g13)
    c: PointOnObject(g10,g13)
    c: PointOnObject(g11,g13)
    c: PointOnObject(g12,g13)
    c: Coincident(g14,g15)
    c: Coincident(g15,g16)
    c: Coincident(g16,g17)
    c: Coincident(g17,g18)
    c: Coincident(g18,g19)
    c: Coincident(g19,g14)
    c: Equal(g14, g15-g19) x5
    c: PointOnObject(g14,g20)
    c: PointOnObject(g15,g20)
    c: PointOnObject(g16,g20)
    c: PointOnObject(g17,g20)
    c: PointOnObject(g18,g20)
    c: PointOnObject(g19,g20)
    c: Coincident(g21,g6)
    c: Coincident(g21,g13)
    c: Coincident(g22,g21)
    c: Coincident(g22,g20)
    c: Vertical(g22)
    c: Coincident(g23,g22)
    c: Coincident(g23,g21)
    c: Equal(g21,g22)
    c: Equal(g22,g23)
    c: DistanceX(g6,g-1) = 12
    c: Equal(g6,g13)
    c: Equal(g13,g20)
    c: Perpendicular(g21,g1)
    c: Perpendicular(g22,g12)
    c: Perpendicular(g23,g17)
    c: DistanceY(g0,g1) = 7.2
    c: Coincident(g24,g-1)
    c: PointOnObject(g6,g24)
    c: PointOnObject(g13,g24)
FEATURE [Sketcher::SketchObject] Sketch119  label="UpperHub_NutSupport_Sketch"
  AttachmentOffset = pos=(0,0,3.4) rot=(0,0,1;0rad)
  ExternalGeometry = -> [Sketch118]
  FullyConstrained = true
  MapMode = 5
  Placement = pos=(0,0,3.4) rot=(0,0,1;0rad)
  Support = -> [XY_Plane058]
  expr: Constraints[1] = <<Common>>#<<Parameters>>.sec_cpointpos
  expr: Constraints[51] = <<Common>>#<<Parameters>>.sec_collbolt * 1.1
  sketch-geometry (34):
    g0: Circle CenterX=0 CenterY=0 CenterZ=0 NormalX=0 NormalY=0 NormalZ=1 AngleXU=0 Radius=12
    g1: LineSegment StartX=-13.8354 StartY=3.6 StartZ=0 EndX=-7.96462 EndY=0.210512 EndZ=0
    g2: LineSegment StartX=-14.2 StartY=3.38949 StartZ=0 EndX=-14.2 EndY=-3.38949 EndZ=0
    g3: LineSegment StartX=-13.8354 StartY=-3.6 StartZ=0 EndX=-7.96462 EndY=-0.210512 EndZ=0
    g4: LineSegment StartX=3.8 StartY=13.7818 StartZ=0 EndX=3.8 EndY=7.00282 EndZ=0
    g5: LineSegment StartX=4.16462 StartY=13.9923 StartZ=0 EndX=10.0354 EndY=10.6028 EndZ=0
    g6: LineSegment StartX=4.16461 StartY=6.7923 StartZ=0 EndX=10.0354 EndY=10.1818 EndZ=0
    g7: LineSegment StartX=3.8 StartY=-7.00282 StartZ=0 EndX=3.8 EndY=-13.7818 EndZ=0
    g8: LineSegment StartX=4.16464 StartY=-13.9923 StartZ=0 EndX=10.0354 EndY=-10.6028 EndZ=0
    g9: LineSegment StartX=4.16462 StartY=-6.7923 StartZ=0 EndX=10.0354 EndY=-10.1818 EndZ=0
    g10: LineSegment StartX=-14.2 StartY=3.38949 StartZ=0 EndX=-14.0785 EndY=3.6 EndZ=0
    g11: LineSegment StartX=-14.0785 StartY=3.6 StartZ=0 EndX=-13.8354 EndY=3.6 EndZ=0
    g12: LineSegment StartX=-7.96462 StartY=0.210512 StartZ=0 EndX=-7.84308 EndY=8.13e-14 EndZ=0
    g13: LineSegment StartX=-7.84308 StartY=8.13e-14 StartZ=0 EndX=-7.96462 EndY=-0.210512 EndZ=0
    g14: LineSegment StartX=-13.8354 StartY=-3.6 StartZ=0 EndX=-14.0785 EndY=-3.6 EndZ=0
    g15: LineSegment StartX=-14.0785 StartY=-3.6 StartZ=0 EndX=-14.2 EndY=-3.38949 EndZ=0
    g16: LineSegment StartX=3.8 StartY=13.7818 StartZ=0 EndX=3.92154 EndY=13.9923 EndZ=0
    g17: LineSegment StartX=3.92154 StartY=13.9923 StartZ=0 EndX=4.16462 EndY=13.9923 EndZ=0
    g18: LineSegment StartX=10.0354 StartY=10.6028 StartZ=0 EndX=10.1569 EndY=10.3923 EndZ=0
    g19: LineSegment StartX=10.1569 StartY=10.3923 StartZ=0 EndX=10.0354 EndY=10.1818 EndZ=0
    g20: LineSegment StartX=4.16461 StartY=6.7923 StartZ=0 EndX=3.92154 EndY=6.7923 EndZ=0
    g21: LineSegment StartX=3.92154 StartY=6.7923 StartZ=0 EndX=3.8 EndY=7.00282 EndZ=0
    g22: LineSegment StartX=3.8 StartY=-7.00282 StartZ=0 EndX=3.92154 EndY=-6.7923 EndZ=0
    g23: LineSegment StartX=3.92154 StartY=-6.7923 StartZ=0 EndX=4.16462 EndY=-6.7923 EndZ=0
    g24: LineSegment StartX=10.0354 StartY=-10.1818 StartZ=0 EndX=10.1569 EndY=-10.3923 EndZ=0
    g25: LineSegment StartX=10.1569 StartY=-10.3923 StartZ=0 EndX=10.0354 EndY=-10.6028 EndZ=0
    g26: LineSegment StartX=4.16464 StartY=-13.9923 StartZ=0 EndX=3.92154 EndY=-13.9923 EndZ=0
    g27: LineSegment StartX=3.92154 StartY=-13.9923 StartZ=0 EndX=3.8 EndY=-13.7818 EndZ=0
    g28: Circle CenterX=-12 CenterY=4e-16 CenterZ=0 NormalX=0 NormalY=0 NormalZ=1 AngleXU=0 Radius=4.15692
    g29: Circle CenterX=-12 CenterY=4e-16 CenterZ=0 NormalX=0 NormalY=0 NormalZ=1 AngleXU=0 Radius=2.2
    g30: Circle CenterX=6 CenterY=10.3923 CenterZ=0 NormalX=0 NormalY=0 NormalZ=1 AngleXU=0 Radius=4.15692
    g31: Circle CenterX=6 CenterY=-10.3923 CenterZ=0 NormalX=0 NormalY=0 NormalZ=1 AngleXU=0 Radius=4.15692
    g32: Circle CenterX=6 CenterY=10.3923 CenterZ=0 NormalX=0 NormalY=0 NormalZ=1 AngleXU=0 Radius=2.2
    g33: Circle CenterX=6 CenterY=-10.3923 CenterZ=0 NormalX=0 NormalY=0 NormalZ=1 AngleXU=0 Radius=2.2
  constraints (89):
    c: Coincident(g0,g-1)
    c: Radius(g0) = 12
    c: Vertical(g2)
    c: Vertical(g7)
    c: Equal(g2,g3)
    c: Equal(g3,g1)
    c: Vertical(g4)
    c: Equal(g4,g5)
    c: Equal(g5,g6)
    c: Equal(g7,g9)
    c: Equal(g9,g8)
    c: Coincident(g10,g2)
    c: Coincident(g11,g10)
    c: Coincident(g11,g1)
    c: Coincident(g12,g1)
    c: Coincident(g13,g12)
    c: Coincident(g13,g3)
    c: Coincident(g14,g3)
    c: Coincident(g15,g14)
    c: Coincident(g15,g2)
    c: Coincident(g16,g4)
    c: Coincident(g17,g16)
    c: Coincident(g17,g5)
    c: Coincident(g18,g5)
    c: Coincident(g19,g18)
    c: Coincident(g19,g6)
    c: Coincident(g20,g6)
    c: Coincident(g21,g20)
    c: Coincident(g21,g4)
    c: Coincident(g22,g7)
    c: Coincident(g23,g22)
    c: Coincident(g23,g9)
    c: Coincident(g24,g9)
    c: Coincident(g25,g24)
    c: Coincident(g25,g8)
    c: Coincident(g26,g8)
    c: Coincident(g27,g26)
    c: Coincident(g27,g7)
    c: PointOnObject(g2,g-3)
    c: PointOnObject(g1,g-4)
    c: Coincident(g10,g-4)
    c: PointOnObject(g1,g-5)
    c: PointOnObject(g3,g-6)
    c: PointOnObject(g3,g-7)
    c: PointOnObject(g2,g-8)
    c: Coincident(g14,g-8)
    c: Coincident(g12,g-6)
    c: PointOnObject(g-5,g28)
    c: PointOnObject(g-8,g28)
    c: PointOnObject(g-7,g28)
    c: Coincident(g29,g28)
    c: Diameter(g29) = 4.4
    c: Tangent(g2,g29)
    c: Tangent(g1,g29)
    c: Tangent(g3,g29)
    c: Coincident(g32,g30)
    c: Coincident(g33,g31)
    c: Equal(g33,g32)
    c: Equal(g32,g29)
    c: PointOnObject(g5,g-10)
    c: PointOnObject(g4,g-9)
    c: PointOnObject(g5,g-11)
    c: PointOnObject(g6,g-12)
    c: PointOnObject(g6,g-13)
    c: PointOnObject(g4,g-14)
    c: Coincident(g20,g-14)
    c: Coincident(g18,g-12)
    c: Coincident(g16,g-10)
    c: PointOnObject(g9,g-16)
    c: PointOnObject(g9,g-17)
    c: PointOnObject(g8,g-18)
    c: PointOnObject(g8,g-19)
    c: PointOnObject(g7,g-20)
    c: PointOnObject(g7,g-15)
    c: Coincident(g26,g-20)
    c: Coincident(g22,g-16)
    c: Coincident(g24,g-18)
    c: PointOnObject(g16,g30)
    c: PointOnObject(g18,g30)
    c: PointOnObject(g20,g30)
    c: PointOnObject(g22,g31)
    c: PointOnObject(g24,g31)
    c: PointOnObject(g26,g31)
    c: Tangent(g4,g32)
    c: Tangent(g5,g32)
    c: Tangent(g6,g32)
    c: Tangent(g7,g33)
    c: Tangent(g9,g33)
    c: Tangent(g8,g33)
FEATURE [PartDesign::SubShapeBinder] Binder
  BindCopyOnChange = 0
  BindMode = 0
  ClaimChildren = false
  Context = -> Body009 [Binder.]
  Fuse = false
  MakeFace = true
  OffsetFill = false
  OffsetIntersection = false
  OffsetJoinType = 0
  OffsetOpenResult = false
  PartialLoad = false
  Relative = true
  Support = -> [<external Common.FCStd>#Body022062[Sketch289.]]
  _Version = 2
FEATURE [PartDesign::ShapeBinder] ShapeBinder  label="SpiderHub_ShapeBinder_Spider"
  Support = -> [Binder]
  TraceSupport = false
FEATURE [Sketcher::SketchObject] Sketch033  label="UpperHub_Main_Sketch"
  ExternalGeometry = -> [ShapeBinder]
  FullyConstrained = true
  MapMode = 5
  Support = -> [XY_Plane058]
  expr: Constraints[0] = <<Common>>#<<Parameters>>.sec_centralbolt * 1.1
  expr: Constraints[20] = <<Common>>#<<Parameters>>.sec_fillet
  expr: Constraints[23] = <<Common>>#<<Parameters>>.sec_cpointpos
  expr: Constraints[28] = <<Common>>#<<Parameters>>.sec_zrotmax
  expr: Constraints[54] = <<Common>>#<<Parameters>>.sec_collbolt * 1.1
  sketch-geometry (20):
    g0: Circle CenterX=0 CenterY=0 CenterZ=0 NormalX=0 NormalY=0 NormalZ=1 AngleXU=0 Radius=2.75
    g1: LineSegment StartX=-19.1267 StartY=4.61831 StartZ=0 EndX=-4.61831 EndY=19.1267 EndZ=0
    g2: LineSegment StartX=-19.1267 StartY=-4.61831 StartZ=0 EndX=-4.61831 EndY=-19.1267 EndZ=0
    g3: ArcOfCircle CenterX=0 CenterY=0 CenterZ=0 NormalX=0 NormalY=0 NormalZ=1 AngleXU=0 Radius=20 StartAngle=4.53343 EndAngle=8.03294
    g4: ArcOfCircle CenterX=-3.2041 CenterY=17.7125 CenterZ=0 NormalX=0 NormalY=0 NormalZ=1 AngleXU=0 Radius=2 StartAngle=1.74976 EndAngle=2.35619
    g5: ArcOfCircle CenterX=-3.2041 CenterY=-17.7125 CenterZ=0 NormalX=0 NormalY=0 NormalZ=1 AngleXU=0 Radius=2 StartAngle=3.92699 EndAngle=4.53343
    g6: ArcOfCircle CenterX=0 CenterY=0 CenterZ=0 NormalX=0 NormalY=0 NormalZ=1 AngleXU=0 Radius=20 StartAngle=2.96263 EndAngle=3.32055
    g7: ArcOfCircle CenterX=-17.7125 CenterY=-3.2041 CenterZ=0 NormalX=0 NormalY=0 NormalZ=1 AngleXU=0 Radius=2 StartAngle=3.32055 EndAngle=3.92699
    g8: ArcOfCircle CenterX=-17.7125 CenterY=3.2041 CenterZ=0 NormalX=0 NormalY=0 NormalZ=1 AngleXU=0 Radius=2 StartAngle=2.35619 EndAngle=2.96263
    g9: Circle CenterX=0 CenterY=0 CenterZ=0 NormalX=0 NormalY=0 NormalZ=1 AngleXU=0 Radius=12
    g10: LineSegment StartX=-11.7156 StartY=2.59728 StartZ=0 EndX=0 EndY=0 EndZ=0
    g11: LineSegment StartX=0 StartY=0 StartZ=0 EndX=-11.7156 EndY=-2.59728 EndZ=0
    g12: ArcOfCircle CenterX=-11.7156 CenterY=2.59728 CenterZ=0 NormalX=0 NormalY=0 NormalZ=1 AngleXU=0 Radius=2.2 StartAngle=6.06502 EndAngle=9.20661
    g13: ArcOfCircle CenterX=-11.7156 CenterY=-2.59728 CenterZ=0 NormalX=0 NormalY=0 NormalZ=1 AngleXU=0 Radius=2.2 StartAngle=3.35976 EndAngle=6.50135
    g14: ArcOfCircle CenterX=11.7156 CenterY=2.59728 CenterZ=0 NormalX=0 NormalY=0 NormalZ=1 AngleXU=0 Radius=2.2 StartAngle=0.218166 EndAngle=3.35976
    g15: ArcOfCircle CenterX=11.7156 CenterY=-2.59728 CenterZ=0 NormalX=0 NormalY=0 NormalZ=1 AngleXU=0 Radius=2.2 StartAngle=2.92343 EndAngle=6.06502
    g16: ArcOfCircle CenterX=0 CenterY=0 CenterZ=0 NormalX=0 NormalY=0 NormalZ=1 AngleXU=0 Radius=9.8 StartAngle=2.92343 EndAngle=3.35976
    g17: ArcOfCircle CenterX=0 CenterY=0 CenterZ=0 NormalX=0 NormalY=0 NormalZ=1 AngleXU=0 Radius=14.2 StartAngle=2.92343 EndAngle=3.35976
    g18: ArcOfCircle CenterX=0 CenterY=0 CenterZ=0 NormalX=0 NormalY=0 NormalZ=1 AngleXU=0 Radius=9.8 StartAngle=6.06502 EndAngle=6.50135
    g19: ArcOfCircle CenterX=0 CenterY=0 CenterZ=0 NormalX=0 NormalY=0 NormalZ=1 AngleXU=0 Radius=14.2 StartAngle=6.06502 EndAngle=6.50135
  constraints (55):
    c: Diameter(g0) = 5.5
    c: Equal(g1,g2)
    c: PointOnObject(g1,g-5)
    c: PointOnObject(g2,g-4)
    c: Coincident(g3,g0)
    c: Coincident(g0,g-3)
    c: Equal(g3,g-3)
    c: Tangent(g1,g4) = 1.5708
    c: Tangent(g2,g5) = -1.5708
    c: Tangent(g3,g5) = -1.5708
    c: Parallel(g2,g-4)
    c: Parallel(g1,g-5)
    c: Equal(g4,g5)
    c: Tangent(g3,g4) = -1.5708
    c: Coincident(g6,g0)
    c: PointOnObject(g6,g-3)
    c: Tangent(g8,g1) = 1.5708
    c: Tangent(g8,g6) = -1.5708
    c: Tangent(g7,g6) = -1.5708
    c: Tangent(g7,g2) = -1.5708
    c: Radius(g8) = 2
    c: Equal(g4,g8)
    c: Coincident(g9,g0)
    c: Radius(g9) = 12
    c: PointOnObject(g10,g9)
    c: Coincident(g10,g0)
    c: Coincident(g11,g0)
    c: Symmetric(g10,g11,g-1)
    c: Angle(g10,g11) = 0.436332
    c: Coincident(g12,g10)
    c: PointOnObject(g12,g10)
    c: Coincident(g13,g11)
    c: PointOnObject(g13,g11)
    c: PointOnObject(g14,g9)
    c: PointOnObject(g15,g9)
    c: Equal(g13,g15)
    c: Equal(g15,g14)
    c: Coincident(g16,g0)
    c: Coincident(g16,g12)
    c: Coincident(g16,g13)
    c: Coincident(g17,g0)
    c: Coincident(g17,g12)
    c: Coincident(g17,g13)
    c: Coincident(g18,g0)
    c: Coincident(g18,g14)
    c: Coincident(g18,g15)
    c: Coincident(g19,g0)
    c: Coincident(g19,g14)
    c: Coincident(g19,g15)
    c: PointOnObject(g12,g10)
    c: PointOnObject(g14,g11)
    c: PointOnObject(g14,g11)
    c: PointOnObject(g14,g11)
    c: PointOnObject(g15,g10)
    c: Diameter(g13) = 4.4
FEATURE [PartDesign::Pad] Pad009  label="UpperHub_Main"
  Direction = (0,0,1)
  Length = 20
  Length2 = 100
  Profile = -> Sketch033
  Type = 0
  expr: Length = <<Common>>#<<Parameters>>.sec_stalkheight
FEATURE [Sketcher::SketchObject] Sketch070  label="UpperHub_CounterBore_Sketch"
  ExternalGeometry = -> [ShapeBinder]
  FullyConstrained = true
  MapMode = 5
  Placement = pos=(0,0,20) rot=(0,0,1;0rad)
  Support = -> [DatumPlane019]
  expr: Constraints[0] = <<Common>>#<<Parameters>>.sec_cpointpos
  expr: Constraints[11] = <<Common>>#<<Parameters>>.sec_collbolt
  expr: Constraints[12] = <<Common>>#<<Parameters>>.sec_zrotmax
  expr: Constraints[73] = <<Common>>#<<Parameters>>.sec_fillet
  sketch-geometry (29):
    g0: Circle CenterX=0 CenterY=0 CenterZ=0 NormalX=0 NormalY=0 NormalZ=1 AngleXU=0 Radius=12
    g1: ArcOfCircle CenterX=-11.7156 CenterY=2.59728 CenterZ=0 NormalX=0 NormalY=0 NormalZ=1 AngleXU=0 Radius=4 StartAngle=6.06502 EndAngle=7.85398
    g2: ArcOfCircle CenterX=-11.7156 CenterY=-2.59728 CenterZ=0 NormalX=0 NormalY=0 NormalZ=1 AngleXU=0 Radius=4 StartAngle=4.71239 EndAngle=6.50135
    g3: LineSegment StartX=0 StartY=0 StartZ=0 EndX=-11.7156 EndY=2.59728 EndZ=0
    g4: LineSegment StartX=0 StartY=0 StartZ=0 EndX=-11.7156 EndY=-2.59728 EndZ=0
    g5: ArcOfCircle CenterX=0 CenterY=0 CenterZ=0 NormalX=0 NormalY=0 NormalZ=1 AngleXU=0 Radius=8 StartAngle=2.92343 EndAngle=3.35976
    g6: ArcOfCircle CenterX=11.7156 CenterY=2.59728 CenterZ=0 NormalX=0 NormalY=0 NormalZ=1 AngleXU=0 Radius=4 StartAngle=1.5708 EndAngle=3.35976
    g7: ArcOfCircle CenterX=11.7156 CenterY=-2.59728 CenterZ=0 NormalX=0 NormalY=0 NormalZ=1 AngleXU=0 Radius=4 StartAngle=2.92343 EndAngle=4.71239
    g8: ArcOfCircle CenterX=0 CenterY=0 CenterZ=0 NormalX=0 NormalY=0 NormalZ=1 AngleXU=0 Radius=8 StartAngle=6.06502 EndAngle=6.50135
    g9: LineSegment StartX=-11.7156 StartY=6.59728 StartZ=0 EndX=-12.3194 EndY=6.59728 EndZ=0
    g10: LineSegment StartX=-11.7156 StartY=-6.59728 StartZ=0 EndX=-12.3194 EndY=-6.59728 EndZ=0
    g11: LineSegment StartX=11.7156 StartY=-6.59728 StartZ=0 EndX=15.8141 EndY=-6.59728 EndZ=0
    g12: LineSegment StartX=11.7156 StartY=6.59728 StartZ=0 EndX=15.8141 EndY=6.59728 EndZ=0
    g13: LineSegment StartX=-11.7156 StartY=6.59728 StartZ=0 EndX=-11.7156 EndY=-6.59728 EndZ=0
    g14: LineSegment StartX=11.7156 StartY=6.59728 StartZ=0 EndX=11.7156 EndY=-6.59728 EndZ=0
    g15: LineSegment StartX=-21 StartY=10.0115 StartZ=0 EndX=-21 EndY=-10.0115 EndZ=0
    g16: ArcOfCircle CenterX=-12.3194 CenterY=8.59728 CenterZ=0 NormalX=0 NormalY=0 NormalZ=1 AngleXU=0 Radius=2 StartAngle=2.35619 EndAngle=4.71239
    g17: ArcOfCircle CenterX=15.8141 CenterY=8.59728 CenterZ=0 NormalX=0 NormalY=0 NormalZ=1 AngleXU=0 Radius=2 StartAngle=4.71239 EndAngle=6.78113
    g18: ArcOfCircle CenterX=15.8141 CenterY=-8.59728 CenterZ=0 NormalX=0 NormalY=0 NormalZ=1 AngleXU=0 Radius=2 StartAngle=5.78523 EndAngle=7.85398
    g19: LineSegment StartX=17.5713 StartY=9.55252 StartZ=0 EndX=21 EndY=9.55252 EndZ=0
    g20: LineSegment StartX=17.5713 StartY=-9.55254 StartZ=0 EndX=21 EndY=-9.55254 EndZ=0
    g21: LineSegment StartX=21 StartY=-9.55254 StartZ=0 EndX=21 EndY=9.55252 EndZ=0
    g22: GeomPoint X=21 Y=0 Z=0
    g23: GeomPoint X=20 Y=0 Z=0
    g24: GeomPoint X=-20 Y=0 Z=0
    g25: GeomPoint X=-21 Y=0 Z=0
    g26: LineSegment StartX=-13.7336 StartY=10.0115 StartZ=0 EndX=-21 EndY=10.0115 EndZ=0
    g27: LineSegment StartX=-13.7336 StartY=-10.0115 StartZ=0 EndX=-21 EndY=-10.0115 EndZ=0
    g28: ArcOfCircle CenterX=-12.3194 CenterY=-8.59728 CenterZ=0 NormalX=0 NormalY=0 NormalZ=1 AngleXU=0 Radius=2 StartAngle=1.5708 EndAngle=3.92699
  constraints (81):
    c: Radius(g0) = 12
    c: Coincident(g0,g-1)
    c: PointOnObject(g1,g0)
    c: Coincident(g3,g-1)
    c: Coincident(g3,g1)
    c: Coincident(g4,g-1)
    c: Coincident(g4,g2)
    c: Symmetric(g1,g2,g-1)
    c: Coincident(g5,g-1)
    c: Coincident(g5,g1)
    c: Coincident(g5,g2)
    c: Radius(g1) = 4
    c: Angle(g3,g4) = 0.436332
    c: PointOnObject(g1,g3)
    c: PointOnObject(g2,g4)
    c: PointOnObject(g6,g0)
    c: PointOnObject(g7,g0)
    c: Coincident(g8,g5)
    c: Coincident(g8,g6)
    c: Coincident(g8,g7)
    c: Equal(g1,g6)
    c: PointOnObject(g6,g4)
    c: PointOnObject(g6,g4)
    c: PointOnObject(g7,g3)
    c: PointOnObject(g7,g3)
    c: Coincident(g9,g1)
    c: Horizontal(g9)
    c: Coincident(g10,g2)
    c: Horizontal(g10)
    c: Coincident(g11,g7)
    c: Horizontal(g11)
    c: Coincident(g12,g6)
    c: Horizontal(g12)
    c: Coincident(g13,g1)
    c: Coincident(g13,g2)
    c: Vertical(g13)
    c: PointOnObject(g1,g13)
    c: Coincident(g14,g6)
    c: Coincident(g14,g7)
    c: Vertical(g14)
    c: PointOnObject(g6,g14)
    c: Vertical(g15)
    c: Coincident(g19,g17)
    c: Horizontal(g19)
    c: Coincident(g20,g18)
    c: Coincident(g21,g20)
    c: Coincident(g21,g19)
    c: Vertical(g21)
    c: Horizontal(g20)
    c: PointOnObject(g18,g-3)
    c: PointOnObject(g17,g-3)
    c: Tangent(g17,g-3)
    c: Tangent(g18,g-3)
    c: Tangent(g18,g11) = 1.5708
    c: Tangent(g17,g12) = -1.5708
    c: PointOnObject(g22,g21)
    c: PointOnObject(g23,g-3)
    c: PointOnObject(g24,g-3)
    c: PointOnObject(g25,g15)
    c: PointOnObject(g25,g-1)
    c: PointOnObject(g24,g-1)
    c: DistanceX(g25,g24) = 1
    c: PointOnObject(g23,g-1)
    c: PointOnObject(g22,g-1)
    c: DistanceX(g23,g22) = 1
    c: PointOnObject(g27,g-5)
    c: PointOnObject(g16,g-4)
    c: Coincident(g26,g16)
    c: Coincident(g26,g15)
    c: Coincident(g27,g15)
    c: Horizontal(g27)
    c: Horizontal(g26)
    c: Tangent(g16,g-4)
    c: Radius(g16) = 2
    c: Tangent(g16,g9) = 1.5708
    c: Coincident(g28,g27)
    c: Tangent(g28,g-5)
    c: Tangent(g28,g10) = -1.5708
    c: Equal(g28,g16)
    c: Equal(g16,g17)
    c: Equal(g17,g18)
FEATURE [PartDesign::Plane] DatumPlane021  label="UpperHub_DatumPlane_SpiderHole"
  Length = 82.6027
  MapMode = 14
  Placement = pos=(-11.8725,-11.8725,0) rot=(0.862856,-0.357407,-0.357407;1.71777rad)
  ResizeMode = 0
  Support = -> [ShapeBinder,Z_Axis058]
  Width = 61.8921
FEATURE [Sketcher::SketchObject] Sketch071  label="UpperHub_SpiderHole_Sketch"
  ExternalGeometry = -> [ShapeBinder]
  FullyConstrained = true
  MapMode = 5
  Placement = pos=(-11.8725,-11.8725,0) rot=(0.862856,-0.357407,-0.357407;1.71777rad)
  Support = -> [DatumPlane021]
  expr: Constraints[0] = <<Common>>#<<Parameters>>.sec_collbolt
  expr: Constraints[3] = <<Common>>#<<Parameters>>.sec_stalkheight / 4
  expr: Constraints[4] = <<Common>>#<<Parameters>>.sec_stalkheight / 4
  expr: Constraints[5] = <<Common>>#<<Parameters>>.sec_stalkheight / 2
  expr: Constraints[6] = <<Common>>#<<Parameters>>.sec_collbolt * 1.5
  expr: Constraints[8] = <<Common>>#<<Parameters>>.sec_sidebolt * 1.25
  sketch-geometry (3):
    g0: Circle CenterX=5.86674 CenterY=5 CenterZ=0 NormalX=0 NormalY=0 NormalZ=1 AngleXU=0 Radius=2
    g1: Circle CenterX=5.86674 CenterY=15 CenterZ=0 NormalX=0 NormalY=0 NormalZ=1 AngleXU=0 Radius=2
    g2: LineSegment StartX=5.86674 StartY=15 StartZ=0 EndX=5.86674 EndY=0 EndZ=0
  constraints (9):
    c: Diameter(g0) = 4
    c: Equal(g0,g1)
    c: Vertical(g2)
    c: PointOnObject(g0,g2) = 5
    c: DistanceY(g2,g0) = 5
    c: DistanceY(g0,g1) = 10
    c: PointOnObject(g2,g-1) = 6
    c: Coincident(g2,g1)
    c: DistanceX(g2,g-3) = 5
FEATURE [PartDesign::Plane] DatumPlane033  label="UpperHub_DatumPlane_SpiderNut"
  AttachmentOffset = pos=(0,0,-3) rot=(0,0,1;0rad)
  Length = 82.6027
  MapMode = 5
  Placement = pos=(-9.75121,-9.75121,0) rot=(0.862856,-0.357407,-0.357407;1.71777rad)
  ResizeMode = 0
  Support = -> [DatumPlane021]
  Width = 61.8921
  expr: .AttachmentOffset.Base.z = -<<Common>>#<<Parameters>>.sec_fthick
FEATURE [Sketcher::SketchObject] Sketch117  label="UpperHub_SpiderNut_Sketch"
  ExternalGeometry = -> [Sketch071]
  FullyConstrained = true
  MapMode = 5
  Placement = pos=(-9.75121,-9.75121,0) rot=(0.862856,-0.357407,-0.357407;1.71777rad)
  Support = -> [DatumPlane033]
  expr: Constraints[11] = 7 + <<Common>>#<<Parameters>>.acc_FDMtol
  sketch-geometry (18):
    g0: LineSegment StartX=9.51674 StartY=11.35 StartZ=0 EndX=9.51674 EndY=21 EndZ=0
    g1: LineSegment StartX=2.21674 StartY=21 StartZ=0 EndX=2.21674 EndY=11.35 EndZ=0
    g2: Circle CenterX=5.86674 CenterY=15 CenterZ=0 NormalX=0 NormalY=0 NormalZ=1 AngleXU=0 Radius=4.21466
    g3: LineSegment StartX=9.51674 StartY=-1 StartZ=0 EndX=9.51674 EndY=8.65 EndZ=0
    g4: LineSegment StartX=2.21674 StartY=8.65 StartZ=0 EndX=2.21674 EndY=-1 EndZ=0
    g5: Circle CenterX=5.86674 CenterY=5 CenterZ=0 NormalX=0 NormalY=0 NormalZ=1 AngleXU=0 Radius=4.21466
    g6: LineSegment StartX=5.86674 StartY=15 StartZ=0 EndX=5.86674 EndY=10.7853 EndZ=0
    g7: LineSegment StartX=5.86674 StartY=5 StartZ=0 EndX=5.86674 EndY=9.21466 EndZ=0
    g8: LineSegment StartX=2.21674 StartY=-1 StartZ=0 EndX=9.51674 EndY=-1 EndZ=0
    g9: LineSegment StartX=2.21674 StartY=21 StartZ=0 EndX=9.51674 EndY=21 EndZ=0
    g10: LineSegment StartX=2.21674 StartY=11.35 StartZ=0 EndX=9.51674 EndY=11.35 EndZ=0
    g11: LineSegment StartX=2.21674 StartY=8.65 StartZ=0 EndX=9.51674 EndY=8.65 EndZ=0
    g12: LineSegment StartX=5.86674 StartY=5 StartZ=0 EndX=2.21674 EndY=8.65 EndZ=0
    g13: LineSegment StartX=5.86674 StartY=5 StartZ=0 EndX=9.51674 EndY=8.65 EndZ=0
    g14: LineSegment StartX=2.21674 StartY=11.35 StartZ=0 EndX=5.86674 EndY=15 EndZ=0
    g15: LineSegment StartX=5.86674 StartY=15 StartZ=0 EndX=9.51674 EndY=11.35 EndZ=0
    g16: LineSegment StartX=5.86674 StartY=10.7853 StartZ=0 EndX=2.21674 EndY=12.8927 EndZ=0
    g17: LineSegment StartX=5.86674 StartY=10.7853 StartZ=0 EndX=9.51674 EndY=12.8927 EndZ=0
  constraints (46):
    c: PointOnObject(g6,g2)
    c: Coincident(g2,g-3)
    c: PointOnObject(g7,g5)
    c: Coincident(g5,g-4)
    c: Equal(g2,g5)
    c: Vertical(g1)
    c: Vertical(g4)
    c: Vertical(g0)
    c: Coincident(g6,g2)
    c: Coincident(g7,g5)
    c: Vertical(g6)
    c: DistanceX(g1,g0) = 7.3
    c: Vertical(g7)
    c: Vertical(g3)
    c: Coincident(g8,g4)
    c: Coincident(g8,g3)
    c: Coincident(g9,g1)
    c: Coincident(g9,g0)
    c: Horizontal(g9)
    c: Equal(g0,g3)
    c: Horizontal(g8)
    c: DistanceY(g4) = -1
    c: Coincident(g10,g1)
    c: Coincident(g10,g0)
    c: Coincident(g11,g4)
    c: Coincident(g11,g3)
    c: Symmetric(g0,g1,g6)
    c: Symmetric(g3,g4,g7)
    c: Equal(g8,g9)
    c: Coincident(g12,g5)
    c: Coincident(g12,g4)
    c: Coincident(g13,g5)
    c: Coincident(g13,g3)
    c: Coincident(g14,g1)
    c: Coincident(g14,g2)
    c: Coincident(g15,g2)
    c: Coincident(g15,g0)
    c: Perpendicular(g14,g15)
    c: Perpendicular(g13,g12)
    c: Coincident(g16,g6)
    c: Coincident(g17,g6)
    c: PointOnObject(g17,g2)
    c: PointOnObject(g17,g0)
    c: PointOnObject(g16,g1)
    c: PointOnObject(g16,g2)
    c: Equal(g16,g6)
FEATURE [PartDesign::Pocket] Pocket  label="UpperHub_CounterBore"
  BaseFeature = -> Pad009
  Direction = (0,0,-1)
  Length = 12
  Length2 = 100
  Profile = -> Sketch070
  Type = 0
  expr: Length = <<Common>>#<<Parameters>>.sec_stalkheight - <<Common>>#<<Parameters>>.sec_pthick
FEATURE [PartDesign::Hole] Hole  label="UpperHub_SpiderHole"
  BaseFeature = -> Pocket
  CustomThreadClearance = 0
  Depth = 8
  DepthType = 0
  Diameter = 4.5
  DrillForDepth = false
  DrillPoint = 1
  DrillPointAngle = 118
  HoleCutCountersinkAngle = 90
  HoleCutCustomValues = false
  HoleCutDepth = 0
  HoleCutDiameter = 6.1
  HoleCutType = 0
  ModelThread = false
  Profile = -> Sketch071
  Tapered = false
  TaperedAngle = 90
  ThreadClass = 0
  ThreadDepth = 8
  ThreadDepthType = 0
  ThreadDirection = 0
  ThreadFit = 0
  ThreadSize = 11
  ThreadType = 1
  Threaded = false
  UseCustomThreadClearance = false
FEATURE [PartDesign::Pocket] Pocket195  label="UpperHub_SpiderNut"
  BaseFeature = -> Hole
  Direction = (0.707107,0.707107,0)
  Length = 3.5
  Length2 = 5
  Profile = -> Sketch117
  ReferenceAxis = -> Sketch117 [N_Axis]
  Type = 0
  expr: Length = 3.2 + <<Common>>#<<Parameters>>.acc_FDMtol
FEATURE [PartDesign::Mirrored] Mirrored  label="UpperHub_Mirrored"
  BaseFeature = -> Pocket195
  MirrorPlane = -> XZ_Plane058
  Originals = -> [Pocket195,Hole]
FEATURE [PartDesign::CoordinateSystem] Local_CS142  label="LCS_HubSpider_FZ"
  AttacherType = Attacher::AttachEngine3D
  MapMode = 11
  Placement = pos=(-7.72411,-16.0209,15) rot=(0.281085,0.678598,-0.678598;3.68962rad)
  Support = -> [Mirrored]
FEATURE [PartDesign::CoordinateSystem] Local_CS143  label="LCS_HubSpider_AZ"
  AttacherType = Attacher::AttachEngine3D
  MapMode = 11
  Placement = pos=(-7.72411,16.0209,15) rot=(-0.862856,-0.357407,0.357407;1.71777rad)
  Support = -> [Mirrored]
FEATURE [PartDesign::Chamfer] Chamfer006  label="UpperHub_Chamfer"
  Angle = 45
  Base = -> Mirrored [Face2,Face6,Edge49,Edge50,Edge47,Edge48,Edge39,Edge40,Edge41,Edge34,Edge4,Edge111,Edge109,Edge105,Edge107]
  BaseFeature = -> Mirrored
  ChamferType = 0
  FlipDirection = false
  Size = 0.4
  Size2 = 1
  SupportTransform = false
  UseAllEdges = false
FEATURE [PartDesign::Body] Body009  label="SpiderHub_Main"
  Group = -> [Sketch033,Pad009,Sketch070,DatumPlane019,Local_CS062,Local_CS060,Local_CS136,Local_CS055,Sketch071,Local_CS142,Local_CS143,DatumPlane021,Sketch112,ShapeBinder,DatumPlane033,Sketch117,Sketch118,Sketch119,Pocket,Hole,Binder,Pocket195,Mirrored,Chamfer006]
  Origin = -> Origin058
  Placement = pos=(-3.125,0,896) rot=(0,0,1;0rad)
  Tip = -> Chamfer006
  expr: .Placement.Base.x = -<<Common>>#<<Parameters>>.sec_offset_x
  expr: .Placement.Base.z = <<Common>>#<<Parameters>>.datum_sec_upperhub
COMPONENT P2 — recipe-attached ("SecondaryMirror", modeled in this document).
Construction recipe (the document's own serialized feature program — sketch geometry with constraints, then the solid features built on it; lengths are millimeters unless a unit is written):

FEATURE [PartDesign::AdditiveCylinder] Cylinder004  label="SecondaryMirror_Cylinder"
  Angle = 360
  AttacherType = Attacher::AttachEngine3D
  AttachmentOffset = pos=(0,0,-31.25) rot=(0,0,1;0rad)
  FirstAngle = 0
  Height = 79.4706
  MapMode = 5
  Placement = pos=(0,0,-31.25) rot=(0,0,1;0rad)
  Radius = 31.25
  SecondAngle = 0
  Support = -> [XY_Plane054]
  expr: .AttachmentOffset.Base.z = -<<Common>>#<<Parameters>>.sec_mdia / 2
  expr: Height = <<Common>>#<<Parameters>>.sec_mdia + <<Common>>#<<Parameters>>.sec_mthick * sqrt(2)
  expr: Radius = <<Common>>#<<Parameters>>.sec_mdia / 2
FEATURE [Sketcher::SketchObject] Sketch060  label="SecondaryMirror_CutSketch"
  FullyConstrained = true
  MapMode = 5
  Placement = pos=(0,0,0) rot=(1,0,0;1.5708rad)
  Support = -> [XZ_Plane054]
  expr: Constraints[13] = <<Common>>#<<Parameters>>.sec_mdia + <<Common>>#<<Parameters>>.sec_mthick
  expr: Constraints[18] = <<Common>>#<<Parameters>>.sec_mthick
  sketch-geometry (7):
    g0: LineSegment StartX=-37.25 StartY=-37.25 StartZ=0 EndX=37.25 EndY=37.25 EndZ=0
    g1: LineSegment StartX=37.25 StartY=37.25 StartZ=0 EndX=37.25 EndY=-37.25 EndZ=0
    g2: LineSegment StartX=37.25 StartY=-37.25 StartZ=0 EndX=-37.25 EndY=-37.25 EndZ=0
    g3: LineSegment StartX=-37.25 StartY=-20.2794 StartZ=0 EndX=37.25 EndY=54.2206 EndZ=0
    g4: LineSegment StartX=37.25 StartY=54.2206 StartZ=0 EndX=-37.25 EndY=54.2206 EndZ=0
    g5: LineSegment StartX=-37.25 StartY=54.2206 StartZ=0 EndX=-37.25 EndY=-20.2794 EndZ=0
    g6: LineSegment StartX=0 StartY=0 StartZ=0 EndX=-8.48528 EndY=8.48528 EndZ=0
  constraints (19):
    c: Coincident(g1,g0)
    c: Vertical(g1)
    c: Coincident(g2,g1)
    c: Coincident(g4,g3)
    c: Coincident(g5,g3)
    c: PointOnObject(g-1,g0)
    c: Coincident(g0,g2)
    c: Equal(g2,g1)
    c: Equal(g5,g4)
    c: Coincident(g5,g4)
    c: Vertical(g5)
    c: Equal(g4,g2)
    c: Symmetric(g0,g1,g-2)
    c: DistanceX(g2,g2) = 74.5
    c: Symmetric(g4,g3,g-2)
    c: Coincident(g6,g-1)
    c: PointOnObject(g6,g3)
    c: Perpendicular(g0,g6)
    c: Distance(g6) = 12
FEATURE [PartDesign::Pocket] Pocket016  label="SecondaryMirror_Pocket"
  BaseFeature = -> Cylinder004
  Direction = (0,1,2e-16)
  Length = 5
  Length2 = 100
  Midplane = true
  Placement = pos=(0,0,-31.25) rot=(0,0,1;0rad)
  Profile = -> Sketch060
  Type = 1
FEATURE [PartDesign::CoordinateSystem] Local_CS122  label="LCS_SecondaryFace"
  AttacherType = Attacher::AttachEngine3D
  MapMode = 5
  Support = -> [XY_Plane054]
FEATURE [PartDesign::CoordinateSystem] Local_CS140  label="LCS_SecondaryOffset"
  AttacherType = Attacher::AttachEngine3D
  AttachmentOffset = pos=(3.125,0,0) rot=(0,0,1;0rad)
  MapMode = 5
  Placement = pos=(3.125,0,0) rot=(0,0,1;0rad)
  Support = -> [XY_Plane054]
  expr: .AttachmentOffset.Base.x = <<Common>>#<<Parameters>>.sec_offset_x
FEATURE [PartDesign::CoordinateSystem] Local_CS141  label="LCS_SecPadDatum"
  AttacherType = Attacher::AttachEngine3D
  AttachmentOffset = pos=(0,0,19.799) rot=(0,0,1;0rad)
  MapMode = 5
  Placement = pos=(0,0,19.799) rot=(0,0,1;0rad)
  Support = -> [XY_Plane054]
  expr: .AttachmentOffset.Base.z = (<<Common>>#<<Parameters>>.sec_mthick + <<Common>>#<<Parameters>>.sec_mfloat) * sqrt(2)
FEATURE [PartDesign::Body] Body022002  label="SecondaryMirror"
  Group = -> [Cylinder004,Sketch060,Pocket016,Local_CS122,Local_CS140,Local_CS141]
  Origin = -> Origin054
  Placement = pos=(-3.125,0,835) rot=(0,0,1;0rad)
  Tip = -> Pocket016
  expr: .Placement.Base.x = -<<Common>>#<<Parameters>>.sec_offset_x
  expr: .Placement.Base.z = <<Common>>#<<Parameters>>.mirror_distance
COMPONENT P3 — recipe-attached ("TiltPlate", modeled in this document).
Construction recipe (the document's own serialized feature program — sketch geometry with constraints, then the solid features built on it; lengths are millimeters unless a unit is written):

FEATURE [PartDesign::AdditiveCylinder] Cylinder005  label="TiltPlate_Base"
  Angle = 360
  AttacherType = Attacher::AttachEngine3D
  FirstAngle = 0
  Height = 8
  MapMode = 5
  Radius = 20
  SecondAngle = 0
  Support = -> [XY_Plane056]
  expr: Height = <<Common>>#<<Parameters>>.sec_pthick
  expr: Radius = <<Common>>#<<Parameters>>.sec_hubdia / 2
FEATURE [PartDesign::AdditiveSphere] Sphere  label="TiltBall_A"
  Angle1 = -90
  Angle2 = 0
  Angle3 = 360
  AttacherType = Attacher::AttachEngine3D
  AttachmentOffset = pos=(6,10.3923,0) rot=(0,0,1;0rad)
  BaseFeature = -> Cylinder005
  MapMode = 2
  Placement = pos=(6,10.3923,0) rot=(0,0,1;0rad)
  Radius = 4
  Support = -> [XY_Plane056]
  expr: .AttachmentOffset.Base.x = <<Common>>#<<Parameters>>.sec_cpointpos * cos(60 deg)
  expr: .AttachmentOffset.Base.y = <<Common>>#<<Parameters>>.sec_cpointpos * sin(60 deg)
  expr: Radius = <<Common>>#<<Parameters>>.sec_tiltball / 2
FEATURE [PartDesign::AdditiveSphere] Sphere001  label="TiltBall_F"
  Angle1 = -90
  Angle2 = 0
  Angle3 = 360
  AttacherType = Attacher::AttachEngine3D
  AttachmentOffset = pos=(6,-10.3923,0) rot=(0,0,1;0rad)
  BaseFeature = -> Sphere
  MapMode = 5
  Placement = pos=(6,-10.3923,0) rot=(0,0,1;0rad)
  Radius = 4
  Support = -> [XY_Plane056]
  expr: .AttachmentOffset.Base.x = <<Common>>#<<Parameters>>.sec_cpointpos * cos(60 deg)
  expr: .AttachmentOffset.Base.y = -<<Common>>#<<Parameters>>.sec_cpointpos * sin(60 deg)
  expr: Radius = <<Common>>#<<Parameters>>.sec_tiltball / 2
FEATURE [PartDesign::Plane] DatumPlane002  label="TiltPlate_DatumPlane_Top"
  AttachmentOffset = pos=(0,0,8) rot=(0,0,1;0rad)
  Length = 60
  MapMode = 5
  Placement = pos=(0,0,8) rot=(0,0,1;0rad)
  ResizeMode = 0
  Support = -> [XY_Plane056]
  Width = 60
  expr: .AttachmentOffset.Base.z = <<Common>>#<<Parameters>>.sec_pthick
FEATURE [Sketcher::SketchObject] Sketch006  label="TiltPlate_Holes_Sketch"
  FullyConstrained = true
  MapMode = 5
  Placement = pos=(0,0,8) rot=(0,0,1;0rad)
  Support = -> [DatumPlane002]
  expr: Constraints[2] = <<Common>>#<<Parameters>>.sec_centralbolt * 1.1
  expr: Constraints[3] = <<Common>>#<<Parameters>>.sec_collbolt * 1.1
  expr: Constraints[6] = <<Common>>#<<Parameters>>.sec_cpointpos
  sketch-geometry (3):
    g0: Circle CenterX=-12 CenterY=0 CenterZ=0 NormalX=0 NormalY=0 NormalZ=1 AngleXU=0 Radius=2.2
    g1: Circle CenterX=12 CenterY=0 CenterZ=0 NormalX=0 NormalY=0 NormalZ=1 AngleXU=0 Radius=2.2
    g2: Circle CenterX=0 CenterY=0 CenterZ=0 NormalX=0 NormalY=0 NormalZ=1 AngleXU=0 Radius=2.75
  constraints (7):
    c: PointOnObject(g0,g-1)
    c: Coincident(g2,g-1)
    c: Diameter(g2) = 5.5
    c: Diameter(g1) = 4.4
    c: Equal(g1,g0)
    c: Symmetric(g1,g0,g-2)
    c: DistanceX(g0,g2) = 12
FEATURE [PartDesign::Plane] DatumPlane003  label="TiltPlate_DatumPlane_Bottom"
  Length = 60
  MapMode = 5
  ResizeMode = 0
  Support = -> [XY_Plane056]
  Width = 60
FEATURE [PartDesign::Pocket] Pocket004  label="TiltPlate_Holes"
  BaseFeature = -> Sphere001
  Direction = (0,0,-1)
  Length = 5
  Length2 = 100
  Placement = pos=(6,-10.3923,0) rot=(0,0,1;0rad)
  Profile = -> Sketch006
  Type = 1
FEATURE [Sketcher::SketchObject] Sketch063  label="TiltPlate_Hex_Sketch"
  FullyConstrained = true
  MapMode = 5
  Support = -> [DatumPlane003]
  expr: Constraints[3] = <<Common>>#<<Parameters>>.sec_cpointpos
  expr: Constraints[4] = <<Common>>#<<Parameters>>.acc_M4Bore
  sketch-geometry (12):
    g0: Circle CenterX=-12 CenterY=0 CenterZ=0 NormalX=0 NormalY=0 NormalZ=1 AngleXU=0 Radius=2.8
    g1: Circle CenterX=12 CenterY=0 CenterZ=0 NormalX=0 NormalY=0 NormalZ=1 AngleXU=0 Radius=2.8
    g2: LineSegment StartX=-17.0912 StartY=0 StartZ=0 EndX=-12 EndY=-5.09117 EndZ=0
    g3: LineSegment StartX=-12 StartY=-5.09117 StartZ=0 EndX=-6.90883 EndY=4.05889e-11 EndZ=0
    g4: LineSegment StartX=-6.90883 StartY=4.05889e-11 StartZ=0 EndX=-12 EndY=5.09117 EndZ=0
    g5: LineSegment StartX=-12 StartY=5.09117 StartZ=0 EndX=-17.0912 EndY=0 EndZ=0
    g6: Circle CenterX=-12 CenterY=0 CenterZ=0 NormalX=0 NormalY=0 NormalZ=1 AngleXU=0 Radius=5.09117
    g7: LineSegment StartX=17.0912 StartY=0 StartZ=0 EndX=12 EndY=5.09117 EndZ=0
    g8: LineSegment StartX=12 StartY=5.09117 StartZ=0 EndX=6.90883 EndY=9e-16 EndZ=0
    g9: LineSegment StartX=6.90883 StartY=8e-16 StartZ=0 EndX=12 EndY=-5.09117 EndZ=0
    g10: LineSegment StartX=12 StartY=-5.09117 StartZ=0 EndX=17.0912 EndY=0 EndZ=0
    g11: Circle CenterX=12 CenterY=0 CenterZ=0 NormalX=0 NormalY=0 NormalZ=1 AngleXU=0 Radius=5.09117
  constraints (33):
    c: PointOnObject(g0,g-1)
    c: Equal(g0,g1)
    c: Symmetric(g1,g0,g-2)
    c: DistanceX(g0,g-1) = 12
    c: Diameter(g0) = 5.6
    c: Coincident(g2,g3)
    c: Coincident(g3,g4)
    c: Coincident(g4,g5)
    c: Coincident(g5,g2)
    c: Equal(g2,g3)
    c: Equal(g2,g4)
    c: Equal(g2,g5)
    c: PointOnObject(g2,g6)
    c: PointOnObject(g3,g6)
    c: PointOnObject(g4,g6)
    c: PointOnObject(g5,g6)
    c: Coincident(g6,g0)
    c: PointOnObject(g5,g-1)
    c: Coincident(g7,g8)
    c: Coincident(g8,g9)
    c: Coincident(g9,g10)
    c: Coincident(g10,g7)
    c: Equal(g7,g8)
    c: Equal(g7,g9)
    c: Equal(g7,g10)
    c: PointOnObject(g7,g11)
    c: PointOnObject(g8,g11)
    c: PointOnObject(g9,g11)
    c: PointOnObject(g10,g11)
    c: Coincident(g11,g1)
    c: PointOnObject(g10,g-1)
    c: Distance(g4) = 7.2
    c: Equal(g11,g6)
FEATURE [PartDesign::Pocket] Pocket005  label="TiltPlate_Hex"
  BaseFeature = -> Pocket004
  Direction = (0,0,-1)
  Length = 4
  Length2 = 100
  Placement = pos=(6,-10.3923,0) rot=(0,0,1;0rad)
  Profile = -> Sketch063
  Reversed = true
  Type = 0
FEATURE [PartDesign::CoordinateSystem] Local_CS124  label="LCS_TiltPlate_Bottom"
  AttacherType = Attacher::AttachEngine3D
  MapMode = 5
  Support = -> [DatumPlane003]
FEATURE [PartDesign::CoordinateSystem] Local_CS125  label="LCS_TiltPlate_Top"
  AttacherType = Attacher::AttachEngine3D
  MapMode = 5
  Placement = pos=(0,0,8) rot=(0,0,1;0rad)
  Support = -> [DatumPlane002]
FEATURE [PartDesign::CoordinateSystem] Local_CS126  label="LCS_Nut_Tilt"
  AttacherType = Attacher::AttachEngine3D
  MapMode = 11
  Placement = pos=(-12,0,4) rot=(0,0,1;1.5708rad)
  Support = -> [Pocket005]
FEATURE [PartDesign::CoordinateSystem] Local_CS127  label="LCS_Nut_Zrot"
  AttacherType = Attacher::AttachEngine3D
  MapMode = 11
  Placement = pos=(12,0,4) rot=(0,0,1;1.5708rad)
  Support = -> [Pocket005]
FEATURE [Sketcher::SketchObject] Sketch124  label="TiltPlate_Ext_Sketch"
  FullyConstrained = true
  MapMode = 5
  Placement = pos=(0,0,8) rot=(0,0,1;0rad)
  Support = -> [DatumPlane002]
  expr: Constraints[2] = <<Common>>#<<Parameters>>.sec_centralbolt * 1.1
  expr: Constraints[3] = <<Common>>#<<Parameters>>.sec_centralbolt * 1.1 + <<Common>>#<<Parameters>>.sec_pthick
  sketch-geometry (2):
    g0: Circle CenterX=0 CenterY=0 CenterZ=0 NormalX=0 NormalY=0 NormalZ=1 AngleXU=0 Radius=6.75
    g1: Circle CenterX=0 CenterY=0 CenterZ=0 NormalX=0 NormalY=0 NormalZ=1 AngleXU=0 Radius=2.75
  constraints (4):
    c: Coincident(g0,g-1)
    c: Coincident(g1,g0)
    c: Diameter(g1) = 5.5
    c: Diameter(g0) = 13.5
FEATURE [PartDesign::Chamfer] Chamfer005  label="TiltPlate_Chamfer"
  Angle = 45
  Base = -> Pocket005 [Face3,Edge2,Edge9,Edge11,Edge12,Edge13,Edge10,Edge7,Edge8,Edge5,Edge6]
  BaseFeature = -> Pocket005
  ChamferType = 0
  FlipDirection = false
  Placement = pos=(6,-10.3923,0) rot=(0,0,1;0rad)
  Size = 0.4
  Size2 = 1
  SupportTransform = false
  UseAllEdges = false
FEATURE [PartDesign::Body] Body022003  label="TiltPlate"
  Group = -> [Cylinder005,Sphere,Sphere001,Sketch006,DatumPlane002,DatumPlane003,Pocket004,Sketch063,Pocket005,Local_CS124,Local_CS125,Local_CS126,Local_CS127,Sketch124,Chamfer005]
  Origin = -> Origin056
  Placement = pos=(-3.125,0,888) rot=(0,0,1;0rad)
  Tip = -> Chamfer005
  expr: .Placement.Base.x = -<<Common>>#<<Parameters>>.sec_offset_x
  expr: .Placement.Base.z = <<Common>>#<<Parameters>>.datum_sec_tiltplate
COMPONENT P4 — recipe-attached ("MirrorCap", modeled in this document).
Construction recipe (the document's own serialized feature program — sketch geometry with constraints, then the solid features built on it; lengths are millimeters unless a unit is written):

FEATURE [PartDesign::AdditiveCylinder] Cylinder009  label="MirrorCap_Body"
  Angle = 360
  AttacherType = Attacher::AttachEngine3D
  AttachmentOffset = pos=(0,0,-45.25) rot=(0,0,1;0rad)
  FirstAngle = 0
  Height = 73.3279
  MapMode = 5
  Placement = pos=(0,0,-45.25) rot=(0,0,1;0rad)
  Radius = 33.4
  SecondAngle = 0
  Support = -> [XY_Plane078]
  expr: .AttachmentOffset.Base.z = -<<Common>>#<<Parameters>>.sec_mdia / 2 - <<Common>>#<<Parameters>>.sec_mthick - <<Common>>#<<Parameters>>.sec_mfloat
  expr: Height = <<Common>>#<<Parameters>>.sec_mdia / 2 + <<Common>>#<<Parameters>>.sec_mthick + <<Common>>#<<Parameters>>.sec_padheight - <<Common>>#<<Parameters>>.sec_mtvar / 2 + <<Common>>#<<Parameters>>.sec_mfloat
  expr: Radius = <<Common>>#<<Parameters>>.sec_mdia / 2 + 0.7 / 2 + <<Common>>#<<Parameters>>.sec_thinwall
FEATURE [Sketcher::SketchObject] Sketch127  label="MirrorCap_Cavity_Sketch"
  FullyConstrained = true
  MapMode = 5
  Support = -> [XY_Plane078]
  expr: Constraints[10] = <<Common>>#<<Parameters>>.sec_hubdia * 0.75 + 0.5
  expr: Constraints[26] = <<Common>>#<<Parameters>>.sec_hubdia * 0.75 + 0.5
  expr: Constraints[4] = <<Common>>#<<Parameters>>.sec_hubdia + 0.5
  sketch-geometry (10):
    g0: LineSegment StartX=-13.3229 StartY=15.25 StartZ=0 EndX=13.3229 EndY=15.25 EndZ=0
    g1: LineSegment StartX=-13.3229 StartY=-15.25 StartZ=0 EndX=13.3229 EndY=-15.25 EndZ=0
    g2: LineSegment StartX=15.25 StartY=13.3229 StartZ=0 EndX=15.25 EndY=-13.3229 EndZ=0
    g3: Circle CenterX=0 CenterY=0 CenterZ=0 NormalX=0 NormalY=0 NormalZ=1 AngleXU=0 Radius=20.25
    g4: ArcOfCircle CenterX=0 CenterY=0 CenterZ=0 NormalX=0 NormalY=0 NormalZ=1 AngleXU=0 Radius=20.25 StartAngle=5.43044 EndAngle=5.56513
    g5: ArcOfCircle CenterX=0 CenterY=0 CenterZ=0 NormalX=0 NormalY=0 NormalZ=1 AngleXU=0 Radius=20.25 StartAngle=0.718056 EndAngle=0.852741
    g6: LineSegment StartX=-13.3229 StartY=15.25 StartZ=0 EndX=-13.3229 EndY=-15.25 EndZ=0
    g7: ArcOfCircle CenterX=0 CenterY=0 CenterZ=0 NormalX=0 NormalY=0 NormalZ=1 AngleXU=0 Radius=20.25 StartAngle=2.28885 EndAngle=2.42354
    g8: ArcOfCircle CenterX=0 CenterY=0 CenterZ=0 NormalX=0 NormalY=0 NormalZ=1 AngleXU=0 Radius=20.25 StartAngle=3.85965 EndAngle=3.99433
    g9: LineSegment StartX=-15.25 StartY=13.3229 StartZ=0 EndX=-15.25 EndY=-13.3229 EndZ=0
  constraints (27):
    c: Horizontal(g0)
    c: Horizontal(g1)
    c: Vertical(g2)
    c: Coincident(g3,g-1)
    c: Diameter(g3) = 40.5
    c: Coincident(g4,g1)
    c: Coincident(g4,g2)
    c: Coincident(g5,g2)
    c: Coincident(g5,g0)
    c: Equal(g4,g3)
    c: DistanceY(g1,g0) = 30.5
    c: Coincident(g6,g0)
    c: Coincident(g6,g1)
    c: Vertical(g6)
    c: Coincident(g7,g4)
    c: Coincident(g7,g0)
    c: Coincident(g8,g4)
    c: Coincident(g8,g1)
    c: Coincident(g9,g7)
    c: Coincident(g9,g8)
    c: Vertical(g9)
    c: Equal(g7,g8)
    c: Equal(g8,g3)
    c: Coincident(g4,g5)
    c: Coincident(g4,g-1)
    c: Symmetric(g7,g2,g-2)
    c: DistanceX(g7,g2) = 30.5
FEATURE [PartDesign::Pocket] Pocket068  label="MirrorCap_Cavity"
  BaseFeature = -> Cylinder009
  Direction = (0,0,-1)
  Length = 5
  Length2 = 100
  Midplane = true
  Placement = pos=(0,0,-45.25) rot=(0,0,1;0rad)
  Profile = -> Sketch127
  Type = 1
FEATURE [Sketcher::SketchObject] Sketch129  label="MirrorCap_Counterbore_Sketch"
  AttachmentOffset = pos=(0,0,19.5) rot=(0,0,1;0rad)
  FullyConstrained = true
  MapMode = 5
  Placement = pos=(0,-19.5,-4.3e-15) rot=(1,0,0;1.5708rad)
  Support = -> [XZ_Plane078]
  expr: .AttachmentOffset.Base.z = <<Common>>#<<Parameters>>.sec_hubdia * 0.75 / 2 + <<Common>>#<<Parameters>>.sec_pthick / 2 + 0.5
  expr: Constraints[10] = <<Common>>#<<Parameters>>.sec_collbolt * 2
  expr: Constraints[11] = <<Common>>#<<Parameters>>.sec_mtvar
  expr: Constraints[15] = <<Common>>#<<Parameters>>.sec_mtvar + <<Common>>#<<Parameters>>.sec_hubdia / 4
  sketch-geometry (7):
    g0: ArcOfCircle CenterX=-8e-16 CenterY=16 CenterZ=0 NormalX=0 NormalY=0 NormalZ=1 AngleXU=0 Radius=4 StartAngle=2e-16 EndAngle=3.14159
    g1: ArcOfCircle CenterX=-1e-16 CenterY=12 CenterZ=0 NormalX=0 NormalY=0 NormalZ=1 AngleXU=0 Radius=4 StartAngle=3.14159 EndAngle=6.28319
    g2: LineSegment StartX=-4 StartY=16 StartZ=0 EndX=-4 EndY=12 EndZ=0
    g3: LineSegment StartX=4 StartY=16 StartZ=0 EndX=4 EndY=12 EndZ=0
    g4: LineSegment StartX=-4 StartY=16 StartZ=0 EndX=4 EndY=12 EndZ=0
    g5: LineSegment StartX=4 StartY=16 StartZ=0 EndX=-4 EndY=12 EndZ=0
    g6: GeomPoint X=0 Y=14 Z=0
  constraints (16):
    c: Tangent(g0,g3) = 1.5708
    c: Tangent(g0,g2) = -1.5708
    c: Tangent(g2,g1) = -1.5708
    c: Tangent(g3,g1) = 1.5708
    c: Vertical(g2)
    c: Equal(g0,g1)
    c: Coincident(g4,g0)
    c: Coincident(g4,g1)
    c: Coincident(g5,g0)
    c: Coincident(g5,g1)
    c: Diameter(g0) = 8
    c: DistanceY(g3,g3) = 4
    c: PointOnObject(g6,g4)
    c: PointOnObject(g6,g-2)
    c: PointOnObject(g6,g5)
    c: DistanceY(g6) = 14
FEATURE [Sketcher::SketchObject] Sketch134  label="MirrorCap_ClipBolt_Sketch"
  FullyConstrained = true
  MapMode = 5
  Placement = pos=(0,0,0) rot=(0.57735,0.57735,0.57735;2.0944rad)
  Support = -> [YZ_Plane078]
  expr: Constraints[1] = <<Common>>#<<Parameters>>.sec_collbolt * 0.8
  expr: Constraints[2] = -(<<Common>>#<<Parameters>>.sec_hubdia * 0.75 + 0.5) / 2
  sketch-geometry (1):
    g0: Circle CenterX=0 CenterY=-15.25 CenterZ=0 NormalX=0 NormalY=0 NormalZ=1 AngleXU=0 Radius=1.6
  constraints (3):
    c: PointOnObject(g0,g-2)
    c: Diameter(g0) = 3.2
    c: DistanceY(g-1,g0) = -15.25
FEATURE [Sketcher::SketchObject] Sketch135  label="MirrorCap_ClipRecess_Sketch"
  FullyConstrained = true
  MapMode = 5
  Support = -> [XY_Plane078]
  expr: Constraints[12] = <<Common>>#<<Parameters>>.sec_thinwall * 2
  expr: Constraints[8] = <<Common>>#<<Parameters>>.sec_mdia + 0.7
  expr: Constraints[9] = <<Common>>#<<Parameters>>.sec_collbolt * 5.5 + 0.5
  sketch-geometry (5):
    g0: ArcOfCircle CenterX=0 CenterY=0 CenterZ=0 NormalX=0 NormalY=0 NormalZ=1 AngleXU=0 Radius=31.6 StartAngle=2.7776 EndAngle=3.50559
    g1: LineSegment StartX=-35.2 StartY=11.25 StartZ=0 EndX=-29.5296 EndY=11.25 EndZ=0
    g2: LineSegment StartX=-35.2 StartY=-11.25 StartZ=0 EndX=-29.5296 EndY=-11.25 EndZ=0
    g3: LineSegment StartX=-35.2 StartY=11.25 StartZ=0 EndX=-35.2 EndY=-11.25 EndZ=0
    g4: GeomPoint X=-31.6 Y=0 Z=0
  constraints (13):
    c: Coincident(g0,g-1)
    c: Coincident(g1,g0)
    c: Coincident(g2,g0)
    c: Horizontal(g2)
    c: Horizontal(g1)
    c: Coincident(g3,g1)
    c: Coincident(g3,g2)
    c: Symmetric(g2,g1,g-1)
    c: Diameter(g0) = 63.2
    c: DistanceY(g3,g3) = 22.5
    c: PointOnObject(g4,g0)
    c: PointOnObject(g4,g-1)
    c: DistanceX(g1,g4) = 3.6
FEATURE [Sketcher::SketchObject] Sketch139  label="MirrorCap_UpperCavity_Sketch"
  FullyConstrained = true
  MapMode = 5
  Placement = pos=(0,0,0) rot=(1,0,0;1.5708rad)
  Support = -> [XZ_Plane078]
  expr: Constraints[10] = <<Common>>#<<Parameters>>.sec_padheight - <<Common>>#<<Parameters>>.sec_mtvar / 2 + 1
  expr: Constraints[11] = <<Common>>#<<Parameters>>.sec_pthick + 1
  expr: Constraints[2] = (<<Common>>#<<Parameters>>.sec_hubdia + 0.5) / 2
  sketch-geometry (4):
    g0: LineSegment StartX=0 StartY=29.0779 StartZ=0 EndX=-20.25 EndY=29.0779 EndZ=0
    g1: LineSegment StartX=-20.25 StartY=29.0779 StartZ=0 EndX=-20.25 EndY=20.0779 EndZ=0
    g2: LineSegment StartX=-20.25 StartY=20.0779 StartZ=0 EndX=0 EndY=-0.172095 EndZ=0
    g3: LineSegment StartX=0 StartY=-0.172095 StartZ=0 EndX=0 EndY=29.0779 EndZ=0
  constraints (12):
    c: PointOnObject(g0,g-2)
    c: Horizontal(g0)
    c: DistanceX(g0,g0) = 20.25
    c: Coincident(g1,g0)
    c: Vertical(g1)
    c: Coincident(g2,g1)
    c: PointOnObject(g2,g-2)
    c: Coincident(g3,g2)
    c: Coincident(g3,g0)
    c: Angle(g-2,g2) = 0.785398
    c: DistanceY(g0) = 29.0779
    c: DistanceY(g1,g1) = 9
FEATURE [PartDesign::Groove] Groove001  label="MirrorCap_UpperCavity"
  Angle = 90
  Axis = (0,-2e-16,1)
  Base = (0,0,0)
  BaseFeature = -> Pocket068
  Midplane = true
  Placement = pos=(0,0,-45.25) rot=(0,0,1;0rad)
  Profile = -> Sketch139
  ReferenceAxis = -> Sketch139 [V_Axis]
  Reversed = true
FEATURE [Sketcher::SketchObject] Sketch222  label="MirrorCap_ClipBase_Sketch"
  FullyConstrained = true
  MapMode = 5
  Placement = pos=(0,0,0) rot=(1,0,0;1.5708rad)
  Support = -> [XZ_Plane078]
  expr: Constraints[10] = <<Common>>#<<Parameters>>.sec_mthick + <<Common>>#<<Parameters>>.sec_mfloat * sqrt(2)
  expr: Constraints[12] = (<<Common>>#<<Parameters>>.sec_mdia + <<Common>>#<<Parameters>>.sec_thinwall * 2 + 1) / 2
  expr: Constraints[14] = <<Common>>#<<Parameters>>.sec_sidebolt * 3 - (<<Common>>#<<Parameters>>.sec_hubdia * 0.75 + 0.5) / 2
  expr: Constraints[15] = <<Common>>#<<Parameters>>.sec_padheight - <<Common>>#<<Parameters>>.sec_mtvar / 2 + 1
  sketch-geometry (5):
    g0: LineSegment StartX=-33.55 StartY=-3.25 StartZ=0 EndX=-25 EndY=5.3 EndZ=0
    g1: LineSegment StartX=-25 StartY=5.3 StartZ=0 EndX=-25 EndY=29.0779 EndZ=0
    g2: LineSegment StartX=-25 StartY=29.0779 StartZ=0 EndX=-33.55 EndY=29.0779 EndZ=0
    g3: LineSegment StartX=-33.55 StartY=29.0779 StartZ=0 EndX=-33.55 EndY=-3.25 EndZ=0
    g4: LineSegment StartX=-33.55 StartY=-48.3784 StartZ=0 EndX=0 EndY=-14.8284 EndZ=0
  constraints (16):
    c: Coincident(g1,g0)
    c: Vertical(g1)
    c: Coincident(g2,g1)
    c: Horizontal(g2)
    c: Coincident(g3,g2)
    c: Vertical(g3)
    c: Coincident(g0,g3)
    c: DistanceX(g1,g-1) = 25
    c: Angle(g0,g3) = 0.785398
    c: PointOnObject(g4,g-2)
    c: DistanceY(g4,g-1) = 14.8284
    c: Angle(g-2,g4) = 2.35619
    c: DistanceX(g4,g-1) = 33.55
    c: PointOnObject(g4,g3)
    c: DistanceY(g0) = -3.25
    c: DistanceY(g2) = 29.0779
FEATURE [PartDesign::Plane] DatumPlane051  label="MirrorCap_DatumPlane_Rim"
  AttachmentOffset = pos=(0,0,-14.8284) rot=(0,-1,0;0.785398rad)
  Length = 113.969
  MapMode = 5
  Placement = pos=(0,0,-14.8284) rot=(0,-1,0;0.785398rad)
  ResizeMode = 0
  Support = -> [XY_Plane078]
  Width = 82.8741
  expr: .AttachmentOffset.Base.z = -(<<Common>>#<<Parameters>>.sec_mthick + <<Common>>#<<Parameters>>.sec_mfloat * sqrt(2))
FEATURE [Sketcher::SketchObject] Sketch224  label="MirrorCap_OuterBody_Shell_Sketch"
  AttachmentOffset = pos=(19.0066,0,19.0066) rot=(0,0,1;0rad)
  FullyConstrained = true
  MapMode = 5
  Placement = pos=(-3.6e-15,0,12.051) rot=(0,-1,0;0.785398rad)
  Support = -> [DatumPlane051]
  expr: .AttachmentOffset.Base.x = (<<Common>>#<<Parameters>>.sec_mthick + <<Common>>#<<Parameters>>.sec_fthick) / sqrt(2) + <<Common>>#<<Parameters>>.sec_mdia / 2 + 0.7 / 2 + <<Common>>#<<Parameters>>.sec_thinwall - 25
  expr: .AttachmentOffset.Base.z = (<<Common>>#<<Parameters>>.sec_mthick + <<Common>>#<<Parameters>>.sec_fthick) / sqrt(2) + <<Common>>#<<Parameters>>.sec_mdia / 2 + 0.7 / 2 + <<Common>>#<<Parameters>>.sec_thinwall - 25
  expr: Constraints[21] = <<Common>>#<<Parameters>>.sec_sidebolt * 5.5
  expr: Constraints[25] = (<<Common>>#<<Parameters>>.sec_mdia + <<Common>>#<<Parameters>>.sec_thinwall * 2 + 1) / sqrt(2)
  expr: Constraints[6] = 25 * sqrt(2)
  sketch-geometry (14):
    g0: Ellipse CenterX=0 CenterY=0 CenterZ=0 NormalX=0 NormalY=0 NormalZ=1 MajorRadius=35.3553 MinorRadius=25 AngleXU=8.97e-14
    g1: LineSegment StartX=35.3553 StartY=2.9642e-12 StartZ=0 EndX=-35.3553 EndY=-2.9642e-12 EndZ=0
    g2: LineSegment StartX=-1.9485e-12 StartY=25 StartZ=0 EndX=1.9485e-12 EndY=-25 EndZ=0
    g3: GeomPoint X=25 Y=2.2425e-12 Z=0
    g4: GeomPoint X=-25 Y=-2.2434e-12 Z=0
    g5: Circle CenterX=0 CenterY=0 CenterZ=0 NormalX=0 NormalY=0 NormalZ=1 AngleXU=0 Radius=50
    g6: ArcOfEllipse CenterX=0 CenterY=0 CenterZ=0 NormalX=0 NormalY=0 NormalZ=1 MajorRadius=35.3553 MinorRadius=25 AngleXU=5.65e-14 StartAngle=3.59719 EndAngle=8.96918
    g7: LineSegment StartX=35.3553 StartY=2.9642e-12 StartZ=0 EndX=-35.3553 EndY=-2.9642e-12 EndZ=0
    g8: LineSegment StartX=-2.7803e-12 StartY=25 StartZ=0 EndX=2.7803e-12 EndY=-25 EndZ=0
    g9: GeomPoint X=25 Y=1.4125e-12 Z=0
    g10: GeomPoint X=-25 Y=-1.4117e-12 Z=0
    g11: LineSegment StartX=-31.749 StartY=-11 StartZ=0 EndX=-47.4469 EndY=-11 EndZ=0
    g12: LineSegment StartX=-31.749 StartY=11 StartZ=0 EndX=-47.4469 EndY=11 EndZ=0
    g13: LineSegment StartX=-47.4469 StartY=11 StartZ=0 EndX=-47.4469 EndY=-11 EndZ=0
  constraints (20):
    c: InternalAlignment(g1-g4 -> g0) x4
    c: Coincident(g0,g-1)
    c: DistanceY(g2) = 25
    c: DistanceX(g1) = 35.3553
    c: Coincident(g5,g0)
    c: Radius(g5) = 50
    c: InternalAlignment(g7-g10 -> g6) x4
    c: Coincident(g6,g0)
    c: Coincident(g7,g1)
    c: PointOnObject(g6,g0)
    c: Coincident(g11,g6)
    c: Horizontal(g11)
    c: Coincident(g12,g6)
    c: Horizontal(g12)
    c: Symmetric(g6,g6,g-1)
    c: DistanceY(g6,g6) = 22
    c: Coincident(g13,g12)
    c: Coincident(g13,g11)
    c: Vertical(g13)
    c: DistanceX(g12,g5) = 47.4469
FEATURE [Sketcher::SketchObject] Sketch225  label="MirrorCap_OuterBody_Top_Sketch"
  AttachmentOffset = pos=(0,0,31.25) rot=(0,0,1;0rad)
  FullyConstrained = true
  MapMode = 5
  Placement = pos=(0,0,31.25) rot=(0,0,1;0rad)
  Support = -> [XY_Plane078]
  expr: .AttachmentOffset.Base.z = <<Common>>#<<Parameters>>.sec_mdia / 2
  expr: Constraints[0] = <<Common>>#<<Parameters>>.sec_mdia + <<Common>>#<<Parameters>>.sec_thinwall * 2 + 1 + <<Common>>#<<Parameters>>.sec_sidebolt * 2
  expr: Constraints[10] = (<<Common>>#<<Parameters>>.sec_mdia + <<Common>>#<<Parameters>>.sec_thinwall * 2 + 1) / 2
  expr: Constraints[11] = <<Common>>#<<Parameters>>.sec_sidebolt * 5.5
  sketch-geometry (5):
    g0: Circle CenterX=0 CenterY=0 CenterZ=0 NormalX=0 NormalY=0 NormalZ=1 AngleXU=0 Radius=37.55
    g1: ArcOfCircle CenterX=0 CenterY=0 CenterZ=0 NormalX=0 NormalY=0 NormalZ=1 AngleXU=0 Radius=25 StartAngle=3.59719 EndAngle=8.96918
    g2: LineSegment StartX=-22.4499 StartY=11 StartZ=0 EndX=-33.55 EndY=11 EndZ=0
    g3: LineSegment StartX=-33.55 StartY=11 StartZ=0 EndX=-33.55 EndY=-11 EndZ=0
    g4: LineSegment StartX=-33.55 StartY=-11 StartZ=0 EndX=-22.4499 EndY=-11 EndZ=0
  constraints (13):
    c: Diameter(g0) = 75.1
    c: Coincident(g2,g1)
    c: Horizontal(g2)
    c: Coincident(g3,g2)
    c: Coincident(g4,g3)
    c: Coincident(g4,g1)
    c: Horizontal(g4)
    c: Diameter(g1) = 50
    c: Coincident(g0,g1)
    c: Coincident(g0,g-1)
    c: DistanceX(g2,g0) = 33.55
    c: DistanceY(g3,g3) = 22
    c: Symmetric(g2,g3,g-1)
FEATURE [PartDesign::Plane] DatumPlane052  label="MirrorCap_DatumPlane_Pad"
  AttachmentOffset = pos=(0,0,-2) rot=(0,-1,0;0.785398rad)
  Length = 113.969
  MapMode = 5
  Placement = pos=(0,0,-2) rot=(0,-1,0;0.785398rad)
  ResizeMode = 0
  Support = -> [XY_Plane078]
  Width = 82.8741
  expr: .AttachmentOffset.Base.z = -<<Common>>#<<Parameters>>.sec_mfloat
FEATURE [Sketcher::SketchObject] Sketch128  label="MirrorCap_Profile_Sketch"
  ExternalGeometry = -> [DatumPlane052]
  FullyConstrained = true
  MapMode = 5
  Placement = pos=(0,0,0) rot=(1,0,0;1.5708rad)
  Support = -> [XZ_Plane078]
  expr: Constraints[16] = <<Common>>#<<Parameters>>.sec_collbolt * 1.1
  expr: Constraints[17] = <<Common>>#<<Parameters>>.sec_mtvar
  expr: Constraints[18] = <<Common>>#<<Parameters>>.sec_mtvar + <<Common>>#<<Parameters>>.sec_hubdia / 4
  expr: Constraints[22] = <<Common>>#<<Parameters>>.sec_mdia + <<Common>>#<<Parameters>>.sec_thinwall * 2 + 1
  expr: Constraints[27] = (<<Common>>#<<Parameters>>.sec_mthick + <<Common>>#<<Parameters>>.sec_mfloat) * 2
  expr: Constraints[30] = <<Common>>#<<Parameters>>.sec_mthick
  sketch-geometry (13):
    g0: LineSegment StartX=-33.55 StartY=-47.55 StartZ=0 EndX=33.55 EndY=19.55 EndZ=0
    g1: LineSegment StartX=33.55 StartY=19.55 StartZ=0 EndX=33.55 EndY=-75.55 EndZ=0
    g2: LineSegment StartX=33.55 StartY=-75.55 StartZ=0 EndX=-33.55 EndY=-75.55 EndZ=0
    g3: ArcOfCircle CenterX=0 CenterY=16 CenterZ=0 NormalX=0 NormalY=0 NormalZ=1 AngleXU=0 Radius=2.2 StartAngle=1.7913e-12 EndAngle=3.14159
    g4: ArcOfCircle CenterX=2.6e-15 CenterY=12 CenterZ=0 NormalX=0 NormalY=0 NormalZ=1 AngleXU=0 Radius=2.2 StartAngle=3.14159 EndAngle=6.28319
    g5: LineSegment StartX=-2.2 StartY=16 StartZ=0 EndX=-2.2 EndY=12 EndZ=0
    g6: LineSegment StartX=2.2 StartY=16 StartZ=0 EndX=2.2 EndY=12 EndZ=0
    g7: LineSegment StartX=-2.2 StartY=16 StartZ=0 EndX=2.2 EndY=12 EndZ=0
    g8: LineSegment StartX=-2.2 StartY=12 StartZ=0 EndX=2.2 EndY=16 EndZ=0
    g9: GeomPoint X=3.5496e-12 Y=14 Z=0
    g10: GeomPoint X=0 Y=-14 Z=0
    g11: LineSegment StartX=-33.55 StartY=-47.55 StartZ=0 EndX=-33.55 EndY=-75.55 EndZ=0
    g12: GeomPoint X=0 Y=-2 Z=0
  constraints (31):
    c: Coincident(g1,g0)
    c: Vertical(g1)
    c: Coincident(g2,g1)
    c: Tangent(g3,g6) = 1.5708
    c: Tangent(g3,g5) = -1.5708
    c: Tangent(g5,g4) = -1.5708
    c: Tangent(g6,g4) = 1.5708
    c: Vertical(g5)
    c: Equal(g3,g4)
    c: PointOnObject(g3,g-2)
    c: Coincident(g7,g3)
    c: Coincident(g7,g4)
    c: Coincident(g8,g4)
    c: Coincident(g8,g3)
    c: PointOnObject(g9,g7)
    c: PointOnObject(g9,g8)
    c: Diameter(g3) = 4.4
    c: DistanceY(g6,g6) = 4
    c: DistanceY(g-1,g9) = 14
    c: Angle(g-1,g0) = 0.785398
    c: PointOnObject(g10,g0)
    c: PointOnObject(g10,g-2)
    c: DistanceX(g2,g2) = 67.1
    c: Symmetric(g2,g1,g-2)
    c: Coincident(g11,g0)
    c: Coincident(g11,g2)
    c: Vertical(g11)
    c: DistanceY(g11,g11) = 28
    c: PointOnObject(g12,g-3)
    c: PointOnObject(g12,g-2)
    c: DistanceY(g10,g12) = 12
FEATURE [Sketcher::SketchObject] Sketch223  label="MirrorCap_OuterBody_Rim_Sketch"
  AttachmentOffset = pos=(2.12132,0,2.12132) rot=(0,0,1;0rad)
  FullyConstrained = true
  MapMode = 5
  Placement = pos=(-4e-16,0,1) rot=(0,-1,0;0.785398rad)
  Support = -> [DatumPlane052]
  expr: .AttachmentOffset.Base.x = <<Common>>#<<Parameters>>.sec_fthick / sqrt(2)
  expr: .AttachmentOffset.Base.z = <<Common>>#<<Parameters>>.sec_fthick / sqrt(2)
  expr: Constraints[22] = (<<Common>>#<<Parameters>>.sec_mdia + <<Common>>#<<Parameters>>.sec_thinwall * 2 + 1) / sqrt(2)
  expr: Constraints[25] = <<Common>>#<<Parameters>>.sec_sidebolt * 5.5
  expr: Constraints[5] = (<<Common>>#<<Parameters>>.sec_mdia + <<Common>>#<<Parameters>>.sec_thinwall * 2 + 1) / 2
  expr: Constraints[6] = (<<Common>>#<<Parameters>>.sec_mdia + <<Common>>#<<Parameters>>.sec_thinwall * 2 + 1) / sqrt(2)
  sketch-geometry (14):
    g0: Ellipse CenterX=0 CenterY=0 CenterZ=0 NormalX=0 NormalY=0 NormalZ=1 MajorRadius=47.4469 MinorRadius=33.55 AngleXU=0
    g1: LineSegment StartX=47.4469 StartY=-4e-16 StartZ=0 EndX=-47.4469 EndY=4e-16 EndZ=0
    g2: LineSegment StartX=3e-16 StartY=33.55 StartZ=0 EndX=-3e-16 EndY=-33.55 EndZ=0
    g3: GeomPoint X=33.55 Y=0 Z=0
    g4: GeomPoint X=-33.55 Y=3e-16 Z=0
    g5: Circle CenterX=0 CenterY=0 CenterZ=0 NormalX=0 NormalY=0 NormalZ=1 AngleXU=0 Radius=50
    g6: ArcOfEllipse CenterX=0 CenterY=0 CenterZ=0 NormalX=0 NormalY=0 NormalZ=1 MajorRadius=47.4469 MinorRadius=33.55 AngleXU=0 StartAngle=3.47564 EndAngle=9.09073
    g7: LineSegment StartX=47.4469 StartY=-4e-16 StartZ=0 EndX=-47.4469 EndY=4e-16 EndZ=0
    g8: LineSegment StartX=6e-16 StartY=33.55 StartZ=0 EndX=-6e-16 EndY=-33.55 EndZ=0
    g9: GeomPoint X=33.55 Y=0 Z=0
    g10: GeomPoint X=-33.55 Y=0 Z=0
    g11: LineSegment StartX=-44.8242 StartY=11 StartZ=0 EndX=-47.4469 EndY=11 EndZ=0
    g12: LineSegment StartX=-47.4469 StartY=11 StartZ=0 EndX=-47.4469 EndY=-11 EndZ=0
    g13: LineSegment StartX=-47.4469 StartY=-11 StartZ=0 EndX=-44.8242 EndY=-11 EndZ=0
  constraints (20):
    c: InternalAlignment(g1-g4 -> g0) x4
    c: Coincident(g0,g-1)
    c: DistanceY(g2) = 33.55
    c: DistanceX(g1) = 47.4469
    c: Coincident(g5,g0)
    c: Radius(g5) = 50
    c: InternalAlignment(g7-g10 -> g6) x4
    c: Coincident(g6,g5)
    c: Coincident(g11,g6)
    c: Horizontal(g11)
    c: Coincident(g12,g11)
    c: Vertical(g12)
    c: Coincident(g13,g12)
    c: Coincident(g13,g6)
    c: Horizontal(g13)
    c: Symmetric(g6,g6,g-1)
    c: DistanceX(g11,g-1) = 47.4469
    c: Coincident(g7,g1)
    c: PointOnObject(g6,g0)
    c: DistanceY(g12,g12) = 22
FEATURE [PartDesign::SubtractiveLoft] SubtractiveLoft  label="MirrorCap_OuterBody"
  BaseFeature = -> Groove001
  Closed = false
  Placement = pos=(0,0,-45.25) rot=(0,0,1;0rad)
  Profile = -> Sketch223
  Ruled = true
  Sections = -> [Sketch224,Sketch225]
FEATURE [Sketcher::SketchObject] Sketch226  label="MirrorCap_MirrorCavity_Sketch"
  FullyConstrained = true
  MapMode = 5
  Placement = pos=(0,0,-2) rot=(0,-1,0;0.785398rad)
  Support = -> [DatumPlane052]
  expr: Constraints[6] = <<Common>>#<<Parameters>>.sec_mdia / 2 + 0.7 / 2
  expr: Constraints[7] = (<<Common>>#<<Parameters>>.sec_mdia / 2 + 0.7 / 2) * sqrt(2)
  sketch-geometry (5):
    g0: Ellipse CenterX=0 CenterY=0 CenterZ=0 NormalX=0 NormalY=0 NormalZ=1 MajorRadius=44.6891 MinorRadius=31.6 AngleXU=0
    g1: LineSegment StartX=44.6891 StartY=0 StartZ=0 EndX=-44.6891 EndY=0 EndZ=0
    g2: LineSegment StartX=0 StartY=31.6 StartZ=0 EndX=0 EndY=-31.6 EndZ=0
    g3: GeomPoint X=31.6 Y=0 Z=0
    g4: GeomPoint X=-31.6 Y=0 Z=0
  constraints (5):
    c: InternalAlignment(g1-g4 -> g0) x4
    c: Coincident(g0,g-1)
    c: PointOnObject(g1,g-1)
    c: DistanceY(g2) = 31.6
    c: DistanceX(g1) = 44.6891
FEATURE [Sketcher::SketchObject] Sketch227  label="MirrorCap_ClipNut_Sketch"
  ExternalGeometry = -> [Sketch134]
  FullyConstrained = true
  MapMode = 5
  Placement = pos=(0,0,0) rot=(0.57735,0.57735,0.57735;2.0944rad)
  Support = -> [YZ_Plane078]
  sketch-geometry (7):
    g0: LineSegment StartX=3.65 StartY=-17.3573 StartZ=0 EndX=3.65 EndY=-13.1427 EndZ=0
    g1: LineSegment StartX=3.65 StartY=-13.1427 StartZ=0 EndX=0 EndY=-11.0353 EndZ=0
    g2: LineSegment StartX=0 StartY=-11.0353 StartZ=0 EndX=-3.65 EndY=-13.1427 EndZ=0
    g3: LineSegment StartX=-3.65 StartY=-13.1427 StartZ=0 EndX=-3.65 EndY=-17.3573 EndZ=0
    g4: LineSegment StartX=-3.65 StartY=-17.3573 StartZ=0 EndX=-4e-16 EndY=-19.4647 EndZ=0
    g5: LineSegment StartX=-4e-16 StartY=-19.4647 StartZ=0 EndX=3.65 EndY=-17.3573 EndZ=0
    g6: Circle CenterX=0 CenterY=-15.25 CenterZ=0 NormalX=0 NormalY=0 NormalZ=1 AngleXU=0 Radius=4.21466
  constraints (16):
    c: Coincident(g0,g1)
    c: Coincident(g1,g2)
    c: Coincident(g2,g3)
    c: Coincident(g3,g4)
    c: Coincident(g4,g5)
    c: Coincident(g5,g0)
    c: Equal(g0, g1-g5) x5
    c: PointOnObject(g0,g6)
    c: PointOnObject(g1,g6)
    c: PointOnObject(g2,g6)
    c: PointOnObject(g3,g6)
    c: PointOnObject(g4,g6)
    c: PointOnObject(g5,g6)
    c: Coincident(g6,g-3)
    c: PointOnObject(g1,g-2)
    c: DistanceX(g2,g0) = 7.3
FEATURE [PartDesign::CoordinateSystem] Local_CS301  label="LCS_MirrorCap_Upper"
  AttacherType = Attacher::AttachEngine3D
  AttachmentOffset = pos=(0,0,30.0779) rot=(0,0,1;0rad)
  MapMode = 5
  Placement = pos=(0,0,30.0779) rot=(0,0,1;0rad)
  Support = -> [XY_Plane078]
  expr: .AttachmentOffset.Base.z = <<Common>>#<<Parameters>>.sec_padheight
FEATURE [PartDesign::CoordinateSystem] Local_CS302  label="LCS_MirrorCap_Pad"
  AttacherType = Attacher::AttachEngine3D
  MapMode = 5
  Support = -> [XY_Plane078]
FEATURE [Sketcher::SketchObject] Sketch237  label="MirrorCap_MirrorCavity_Path"
  FullyConstrained = true
  MapMode = 5
  Placement = pos=(0,0,0) rot=(1,0,0;1.5708rad)
  Support = -> [XZ_Plane078]
  expr: Constraints[2] = <<Common>>#<<Parameters>>.sec_mdia
  sketch-geometry (1):
    g0: LineSegment StartX=0 StartY=0 StartZ=0 EndX=0 EndY=-62.5 EndZ=0
  constraints (3):
    c: Coincident(g0,g-1)
    c: Vertical(g0)
    c: DistanceY(g0,g0) = 62.5
FEATURE [PartDesign::SubtractivePipe] SubtractivePipe  label="MirrorCap_MirrorCavity_Cut"
  AuxilleryCurvelinear = true
  AuxillerySpineTangent = false
  BaseFeature = -> SubtractiveLoft
  Binormal = (0,0,0)
  Mode = 0
  Placement = pos=(0,0,-45.25) rot=(0,0,1;0rad)
  Profile = -> Sketch226
  Spine = -> Sketch237
  SpineTangent = false
  Transformation = 0
  Transition = 0
FEATURE [PartDesign::Pocket] Pocket151  label="MirrorCap_Profile_Cut"
  BaseFeature = -> SubtractivePipe
  Direction = (0,1,2e-16)
  Length = 5
  Length2 = 100
  Midplane = true
  Placement = pos=(0,0,-45.25) rot=(0,0,1;0rad)
  Profile = -> Sketch128
  Type = 1
FEATURE [PartDesign::Groove] Groove005  label="MirrorCap_ClipBase_Groove"
  Angle = 52.2078
  Axis = (-3e-16,3e-16,1)
  Base = (0,0,0)
  BaseFeature = -> Pocket151
  Midplane = true
  Placement = pos=(0,0,-45.25) rot=(0,0,1;0rad)
  Profile = -> Sketch222
  ReferenceAxis = -> Z_Axis078
  Reversed = true
  expr: Angle = 2 * asin(<<Common>>#<<Parameters>>.sec_sidebolt * 5.5 / 50)
FEATURE [PartDesign::Pocket] Pocket152  label="MirrorCap_ClipRecess_Cut"
  BaseFeature = -> Groove005
  Direction = (0,0,-1)
  Length = 5
  Length2 = 100
  Placement = pos=(0,0,-45.25) rot=(0,0,1;0rad)
  Profile = -> Sketch135
  Type = 1
FEATURE [PartDesign::Hole] Hole052  label="MirrorCap_ClipBolt_Hole"
  BaseFeature = -> Pocket152
  CustomThreadClearance = 0
  Depth = 25
  DepthType = 1
  Diameter = 4.5
  DrillForDepth = false
  DrillPoint = 1
  DrillPointAngle = 118
  HoleCutCountersinkAngle = 90
  HoleCutCustomValues = false
  HoleCutDepth = 0
  HoleCutDiameter = 6.1
  HoleCutType = 0
  ModelThread = false
  Placement = pos=(0,0,-45.25) rot=(0,0,1;0rad)
  Profile = -> Sketch134
  Tapered = false
  TaperedAngle = 90
  ThreadClass = 0
  ThreadDepth = 23.5
  ThreadDepthType = 0
  ThreadDirection = 0
  ThreadFit = 0
  ThreadSize = 11
  ThreadType = 1
  Threaded = false
  UseCustomThreadClearance = false
FEATURE [PartDesign::Pocket] Pocket153  label="MirrorCap_ClipNut_Cut"
  BaseFeature = -> Hole052
  Direction = (-1,2e-16,-3e-16)
  Length = 28.25
  Length2 = 100
  Placement = pos=(0,0,-45.25) rot=(0,0,1;0rad)
  Profile = -> Sketch227
  Type = 0
  expr: Length = <<Common>>#<<Parameters>>.sec_mdia / 2 - <<Common>>#<<Parameters>>.sec_fthick
FEATURE [PartDesign::CoordinateSystem] Local_CS303  label="LCS_MirrorCap_ClipNut"
  AttacherType = Attacher::AttachEngine3D
  MapMode = 11
  Placement = pos=(-28.25,2.9e-15,-15.25) rot=(-0.57735,0.57735,0.57735;4.18879rad)
  Support = -> [Pocket153]
FEATURE [PartDesign::Pocket] Pocket154  label="MirrorCap_Counterbore_Cut"
  BaseFeature = -> Pocket153
  Direction = (0,1,2e-16)
  Length = 5
  Length2 = 100
  Placement = pos=(0,0,-45.25) rot=(0,0,1;0rad)
  Profile = -> Sketch129
  Reversed = true
  Type = 1
FEATURE [PartDesign::Mirrored] Mirrored007  label="MirrorCap_Counterbore_Mirror"
  BaseFeature = -> Pocket154
  MirrorPlane = -> XZ_Plane078
  Originals = -> [Pocket154]
  Placement = pos=(0,0,-45.25) rot=(0,0,1;0rad)
FEATURE [PartDesign::Chamfer] Chamfer  label="MirrorCap_Chamfer"
  Angle = 45
  Base = -> Mirrored007 [Edge31,Edge29,Edge27,Edge26,Edge28,Edge30,Edge32,Edge34,Edge35,Edge33,Edge24,Edge23,Edge22]
  BaseFeature = -> Mirrored007
  ChamferType = 0
  FlipDirection = false
  Placement = pos=(0,0,-45.25) rot=(0,0,1;0rad)
  Size = 0.4
  Size2 = 1
  SupportTransform = false
  UseAllEdges = false
FEATURE [PartDesign::Body] Body022025  label="MirrorCap"
  Group = -> [Cylinder009,Sketch127,Pocket068,Sketch128,Sketch129,Sketch134,Sketch135,Sketch139,Groove001,Sketch222,DatumPlane051,Sketch223,Sketch224,SubtractiveLoft,Sketch225,Sketch226,DatumPlane052,Sketch227,Local_CS301,Local_CS302,Local_CS303,Sketch237,SubtractivePipe,Pocket151,Groove005,Pocket152,Hole052,Pocket153,Pocket154,Mirrored007,Chamfer]
  Origin = -> Origin078
  Placement = pos=(-3.125,0,854.799) rot=(0,0,1;0rad)
  Tip = -> Chamfer
  expr: .Placement.Base.x = -<<Common>>#<<Parameters>>.sec_offset_x
  expr: .Placement.Base.z = <<Common>>#<<Parameters>>.datum_sec_mirrorpad
COMPONENT P5 — recipe-attached ("MirrorOuterPad", modeled in this document).
Construction recipe (the document's own serialized feature program — sketch geometry with constraints, then the solid features built on it; lengths are millimeters unless a unit is written):

FEATURE [Sketcher::SketchObject] Sketch130  label="MirrorOuter_Profile_Sketch"
  FullyConstrained = true
  MapMode = 5
  Placement = pos=(0,0,0) rot=(1,0,0;1.5708rad)
  Support = -> [XZ_Plane079]
  expr: Constraints[16] = <<Common>>#<<Parameters>>.sec_collbolt * 1.1
  expr: Constraints[17] = <<Common>>#<<Parameters>>.sec_mtvar
  expr: Constraints[18] = <<Common>>#<<Parameters>>.sec_mtvar + <<Common>>#<<Parameters>>.sec_hubdia / 4
  expr: Constraints[21] = <<Common>>#<<Parameters>>.sec_mdia + <<Common>>#<<Parameters>>.sec_thinwall * 2 + 1
  expr: Constraints[26] = (<<Common>>#<<Parameters>>.sec_mthick + <<Common>>#<<Parameters>>.sec_mfloat) * 2
  sketch-geometry (12):
    g0: LineSegment StartX=-33.55 StartY=-33.55 StartZ=0 EndX=33.55 EndY=33.55 EndZ=0
    g1: LineSegment StartX=33.55 StartY=33.55 StartZ=0 EndX=33.55 EndY=-61.55 EndZ=0
    g2: LineSegment StartX=33.55 StartY=-61.55 StartZ=0 EndX=-33.55 EndY=-61.55 EndZ=0
    g3: ArcOfCircle CenterX=0 CenterY=16 CenterZ=0 NormalX=0 NormalY=0 NormalZ=1 AngleXU=0 Radius=2.2 StartAngle=1.7906e-12 EndAngle=3.14159
    g4: ArcOfCircle CenterX=2.9e-15 CenterY=12 CenterZ=0 NormalX=0 NormalY=0 NormalZ=1 AngleXU=0 Radius=2.2 StartAngle=3.14159 EndAngle=6.28319
    g5: LineSegment StartX=-2.2 StartY=16 StartZ=0 EndX=-2.2 EndY=12 EndZ=0
    g6: LineSegment StartX=2.2 StartY=16 StartZ=0 EndX=2.2 EndY=12 EndZ=0
    g7: LineSegment StartX=-2.2 StartY=16 StartZ=0 EndX=2.2 EndY=12 EndZ=0
    g8: LineSegment StartX=-2.2 StartY=12 StartZ=0 EndX=2.2 EndY=16 EndZ=0
    g9: GeomPoint X=3.5503e-12 Y=14 Z=0
    g10: GeomPoint X=0 Y=0 Z=0
    g11: LineSegment StartX=-33.55 StartY=-33.55 StartZ=0 EndX=-33.55 EndY=-61.55 EndZ=0
  constraints (28):
    c: Coincident(g1,g0)
    c: Vertical(g1)
    c: Coincident(g2,g1)
    c: Tangent(g3,g6) = 1.5708
    c: Tangent(g3,g5) = -1.5708
    c: Tangent(g5,g4) = -1.5708
    c: Tangent(g6,g4) = 1.5708
    c: Vertical(g5)
    c: Equal(g3,g4)
    c: PointOnObject(g3,g-2)
    c: Coincident(g7,g3)
    c: Coincident(g7,g4)
    c: Coincident(g8,g4)
    c: Coincident(g8,g3)
    c: PointOnObject(g9,g7)
    c: PointOnObject(g9,g8)
    c: Diameter(g3) = 4.4
    c: DistanceY(g6,g6) = 4
    c: DistanceY(g-1,g9) = 14
    c: Angle(g-1,g0) = 0.785398
    c: PointOnObject(g10,g0)
    c: DistanceX(g2,g2) = 67.1
    c: Symmetric(g2,g1,g-2)
    c: Coincident(g11,g0)
    c: Coincident(g11,g2)
    c: Vertical(g11)
    c: DistanceY(g11,g11) = 28
    c: Coincident(g10,g-1)
FEATURE [PartDesign::AdditiveCylinder] Cylinder010  label="MirrorOuter_Body"
  Angle = 360
  AttacherType = Attacher::AttachEngine3D
  AttachmentOffset = pos=(0,0,-43.25) rot=(0,0,1;0rad)
  FirstAngle = 0
  Height = 71.3279
  MapMode = 5
  Placement = pos=(0,0,-43.25) rot=(0,0,1;0rad)
  Radius = 31.25
  SecondAngle = 0
  Support = -> [XY_Plane079]
  expr: .AttachmentOffset.Base.z = -<<Common>>#<<Parameters>>.sec_mdia / 2 - <<Common>>#<<Parameters>>.sec_mthick
  expr: Height = <<Common>>#<<Parameters>>.sec_mdia / 2 + <<Common>>#<<Parameters>>.sec_mthick + <<Common>>#<<Parameters>>.sec_padheight - <<Common>>#<<Parameters>>.sec_mtvar / 2
  expr: Radius = <<Common>>#<<Parameters>>.sec_mdia / 2
FEATURE [Sketcher::SketchObject] Sketch131  label="MirrorOuter_CounterBore_Sketch"
  AttachmentOffset = pos=(0,0,19.5) rot=(0,0,1;0rad)
  FullyConstrained = true
  MapMode = 5
  Placement = pos=(0,-19.5,-4.3e-15) rot=(1,0,0;1.5708rad)
  Support = -> [XZ_Plane079]
  expr: .AttachmentOffset.Base.z = <<Common>>#<<Parameters>>.sec_hubdia * 0.75 / 2 + <<Common>>#<<Parameters>>.sec_pthick / 2 + 0.5
  expr: Constraints[10] = <<Common>>#<<Parameters>>.sec_collbolt * 2
  expr: Constraints[11] = <<Common>>#<<Parameters>>.sec_mtvar
  expr: Constraints[15] = <<Common>>#<<Parameters>>.sec_mtvar + <<Common>>#<<Parameters>>.sec_hubdia / 4
  sketch-geometry (7):
    g0: ArcOfCircle CenterX=1.7e-15 CenterY=16 CenterZ=0 NormalX=0 NormalY=0 NormalZ=1 AngleXU=0 Radius=4 StartAngle=0 EndAngle=3.14159
    g1: ArcOfCircle CenterX=1.7e-15 CenterY=12 CenterZ=0 NormalX=0 NormalY=0 NormalZ=1 AngleXU=0 Radius=4 StartAngle=3.14159 EndAngle=6.28319
    g2: LineSegment StartX=-4 StartY=16 StartZ=0 EndX=-4 EndY=12 EndZ=0
    g3: LineSegment StartX=4 StartY=16 StartZ=0 EndX=4 EndY=12 EndZ=0
    g4: LineSegment StartX=-4 StartY=16 StartZ=0 EndX=4 EndY=12 EndZ=0
    g5: LineSegment StartX=4 StartY=16 StartZ=0 EndX=-4 EndY=12 EndZ=0
    g6: GeomPoint X=0 Y=14 Z=0
  constraints (16):
    c: Tangent(g0,g3) = 1.5708
    c: Tangent(g0,g2) = -1.5708
    c: Tangent(g2,g1) = -1.5708
    c: Tangent(g3,g1) = 1.5708
    c: Vertical(g2)
    c: Equal(g0,g1)
    c: Coincident(g4,g0)
    c: Coincident(g4,g1)
    c: Coincident(g5,g0)
    c: Coincident(g5,g1)
    c: Diameter(g0) = 8
    c: DistanceY(g3,g3) = 4
    c: PointOnObject(g6,g4)
    c: PointOnObject(g6,g-2)
    c: PointOnObject(g6,g5)
    c: DistanceY(g6) = 14
FEATURE [Sketcher::SketchObject] Sketch132  label="MirrorOuter_Cavity_Sketch"
  FullyConstrained = true
  MapMode = 5
  Support = -> [XY_Plane079]
  expr: Constraints[10] = <<Common>>#<<Parameters>>.sec_hubdia * 0.75 + 0.5
  expr: Constraints[26] = <<Common>>#<<Parameters>>.sec_hubdia * 0.75 + 0.5
  expr: Constraints[4] = <<Common>>#<<Parameters>>.sec_hubdia + 0.5
  sketch-geometry (10):
    g0: LineSegment StartX=-13.3229 StartY=15.25 StartZ=0 EndX=13.3229 EndY=15.25 EndZ=0
    g1: LineSegment StartX=-13.3229 StartY=-15.25 StartZ=0 EndX=13.3229 EndY=-15.25 EndZ=0
    g2: LineSegment StartX=15.25 StartY=13.3229 StartZ=0 EndX=15.25 EndY=-13.3229 EndZ=0
    g3: Circle CenterX=0 CenterY=0 CenterZ=0 NormalX=0 NormalY=0 NormalZ=1 AngleXU=0 Radius=20.25
    g4: ArcOfCircle CenterX=0 CenterY=0 CenterZ=0 NormalX=0 NormalY=0 NormalZ=1 AngleXU=0 Radius=20.25 StartAngle=5.43044 EndAngle=5.56513
    g5: ArcOfCircle CenterX=0 CenterY=0 CenterZ=0 NormalX=0 NormalY=0 NormalZ=1 AngleXU=0 Radius=20.25 StartAngle=0.718056 EndAngle=0.852741
    g6: LineSegment StartX=-13.3229 StartY=15.25 StartZ=0 EndX=-13.3229 EndY=-15.25 EndZ=0
    g7: ArcOfCircle CenterX=0 CenterY=0 CenterZ=0 NormalX=0 NormalY=0 NormalZ=1 AngleXU=0 Radius=20.25 StartAngle=2.28885 EndAngle=2.42354
    g8: ArcOfCircle CenterX=0 CenterY=0 CenterZ=0 NormalX=0 NormalY=0 NormalZ=1 AngleXU=0 Radius=20.25 StartAngle=3.85965 EndAngle=3.99433
    g9: LineSegment StartX=-15.25 StartY=13.3229 StartZ=0 EndX=-15.25 EndY=-13.3229 EndZ=0
  constraints (27):
    c: Horizontal(g0)
    c: Horizontal(g1)
    c: Vertical(g2)
    c: Coincident(g3,g-1)
    c: Diameter(g3) = 40.5
    c: Coincident(g4,g1)
    c: Coincident(g4,g2)
    c: Coincident(g5,g2)
    c: Coincident(g5,g0)
    c: Equal(g4,g3)
    c: DistanceY(g1,g0) = 30.5
    c: Coincident(g6,g0)
    c: Coincident(g6,g1)
    c: Vertical(g6)
    c: Coincident(g5,g4)
    c: Coincident(g5,g-1)
    c: Equal(g5,g3)
    c: Coincident(g7,g4)
    c: Coincident(g7,g0)
    c: Coincident(g8,g4)
    c: Coincident(g8,g1)
    c: Coincident(g9,g7)
    c: Coincident(g9,g8)
    c: Vertical(g9)
    c: Symmetric(g7,g2,g-2)
    c: Equal(g7,g8)
    c: DistanceX(g7,g2) = 30.5
FEATURE [PartDesign::Pocket] Pocket071  label="MirrorOuter_Cavity"
  BaseFeature = -> Cylinder010
  Direction = (0,0,-1)
  Length = 5
  Length2 = 100
  Midplane = true
  Placement = pos=(0,0,-43.25) rot=(0,0,1;0rad)
  Profile = -> Sketch132
  Type = 1
FEATURE [Sketcher::SketchObject] Sketch140  label="MirrorOuter_UpperCavity_Sketch"
  AttachmentOffset = pos=(0,0,28.0779) rot=(0,0,1;0rad)
  FullyConstrained = true
  MapMode = 5
  Placement = pos=(0,0,28.0779) rot=(0,0,1;0rad)
  Support = -> [XY_Plane079]
  expr: .AttachmentOffset.Base.z = <<Common>>#<<Parameters>>.sec_padheight - <<Common>>#<<Parameters>>.sec_mtvar / 2
  expr: Constraints[4] = <<Common>>#<<Parameters>>.sec_hubdia + 0.5
  expr: Constraints[5] = <<Common>>#<<Parameters>>.sec_hubdia * 0.75 + 0.5
  sketch-geometry (2):
    g0: ArcOfCircle CenterX=0 CenterY=0 CenterZ=0 NormalX=0 NormalY=0 NormalZ=1 AngleXU=0 Radius=20.25 StartAngle=2.28885 EndAngle=3.99433
    g1: LineSegment StartX=-13.3229 StartY=15.25 StartZ=0 EndX=-13.3229 EndY=-15.25 EndZ=0
  constraints (6):
    c: Coincident(g0,g-1)
    c: Coincident(g1,g0)
    c: Coincident(g1,g0)
    c: Vertical(g1)
    c: Diameter(g0) = 40.5
    c: DistanceY(g1,g1) = 30.5
FEATURE [PartDesign::Pocket] Pocket084  label="MirrorOuter_UpperCavity"
  BaseFeature = -> Pocket071
  Direction = (0,0,-1)
  Length = 8.5
  Length2 = 100
  Placement = pos=(0,0,-43.25) rot=(0,0,1;0rad)
  Profile = -> Sketch140
  Type = 0
  expr: Length = <<Common>>#<<Parameters>>.sec_pthick + 0.5
FEATURE [PartDesign::Pocket] Pocket085  label="MirrorOuter_Profile"
  BaseFeature = -> Pocket084
  Direction = (0,1,2e-16)
  Length = 5
  Length2 = 100
  Midplane = true
  Placement = pos=(0,0,-43.25) rot=(0,0,1;0rad)
  Profile = -> Sketch130
  Type = 1
FEATURE [PartDesign::CoordinateSystem] Local_CS226  label="LCS_MirrorOuter_Upper"
  AttacherType = Attacher::AttachEngine3D
  AttachmentOffset = pos=(0,0,30.0779) rot=(0,0,1;0rad)
  MapMode = 5
  Placement = pos=(0,0,30.0779) rot=(0,0,1;0rad)
  Support = -> [XY_Plane079]
  expr: .AttachmentOffset.Base.z = <<Common>>#<<Parameters>>.sec_padheight
FEATURE [PartDesign::CoordinateSystem] Local_CS228  label="LCS_MirrorOuter_Pad"
  AttacherType = Attacher::AttachEngine3D
  MapMode = 5
  Support = -> [XY_Plane079]
FEATURE [Sketcher::SketchObject] Sketch  label="MirrorOuter_CavityGroove_Sketch"
  ExternalGeometry = -> [Pocket085]
  FullyConstrained = true
  MapMode = 5
  Placement = pos=(0,0,0) rot=(1,0,0;1.5708rad)
  Support = -> [XZ_Plane079]
  sketch-geometry (3):
    g0: LineSegment StartX=-20.25 StartY=19.5779 StartZ=0 EndX=0 EndY=19.5779 EndZ=0
    g1: LineSegment StartX=-20.25 StartY=19.5779 StartZ=0 EndX=0 EndY=-0.672095 EndZ=0
    g2: LineSegment StartX=0 StartY=19.5779 StartZ=0 EndX=0 EndY=-0.672095 EndZ=0
  constraints (8):
    c: Coincident(g0,g-3)
    c: Horizontal(g0)
    c: Coincident(g1,g0)
    c: PointOnObject(g1,g-2)
    c: Angle(g1,g0) = 0.785398
    c: Coincident(g2,g0)
    c: Coincident(g2,g1)
    c: Vertical(g2)
FEATURE [PartDesign::Groove] Groove  label="MirrorOuter_CavityGroove"
  Angle = 90
  Axis = (-3e-16,3e-16,1)
  Base = (0,0,0)
  BaseFeature = -> Pocket085
  Midplane = true
  Placement = pos=(0,0,-43.25) rot=(0,0,1;0rad)
  Profile = -> Sketch
  ReferenceAxis = -> Z_Axis079
  Reversed = true
FEATURE [PartDesign::Pocket] Pocket192  label="MirrorOuter_CounterBore"
  BaseFeature = -> Groove
  Direction = (0,1,2e-16)
  Length = 5
  Length2 = 5
  Placement = pos=(0,0,-43.25) rot=(0,0,1;0rad)
  Profile = -> Sketch131
  ReferenceAxis = -> Sketch131 [N_Axis]
  Reversed = true
  Type = 1
FEATURE [PartDesign::Mirrored] Mirrored009  label="MirrorOuter_Mirrored"
  BaseFeature = -> Pocket192
  MirrorPlane = -> XZ_Plane079
  Originals = -> [Pocket192]
  Placement = pos=(0,0,-43.25) rot=(0,0,1;0rad)
FEATURE [PartDesign::Chamfer] Chamfer003  label="MirrorOuter_Chamfer"
  Angle = 45
  Base = -> Mirrored009 [Edge2,Edge11,Edge27,Edge25,Edge23,Edge21,Edge20,Edge22,Edge24,Edge26]
  BaseFeature = -> Mirrored009
  ChamferType = 0
  FlipDirection = false
  Placement = pos=(0,0,-43.25) rot=(0,0,1;0rad)
  Size = 0.4
  Size2 = 1
  SupportTransform = false
  UseAllEdges = false
FEATURE [PartDesign::Body] Body022026  label="MirrorOuterPad"
  Group = -> [Cylinder010,Sketch132,Pocket071,Sketch130,Sketch131,Sketch140,Pocket084,Pocket085,Local_CS226,Local_CS228,Sketch,Groove,Pocket192,Mirrored009,Chamfer003]
  Origin = -> Origin079
  Placement = pos=(-3.125,0,854.799) rot=(0,0,1;0rad)
  Tip = -> Chamfer003
  expr: .Placement.Base.x = -<<Common>>#<<Parameters>>.sec_offset_x
  expr: .Placement.Base.z = <<Common>>#<<Parameters>>.datum_sec_mirrorpad
COMPONENT P6 — recipe-attached ("SecondaryClip", modeled in this document).
Construction recipe (the document's own serialized feature program — sketch geometry with constraints, then the solid features built on it; lengths are millimeters unless a unit is written):

FEATURE [PartDesign::AdditiveBox] Box  label="SecondaryClip_Base"
  AttacherType = Attacher::AttachEngine3D
  AttachmentOffset = pos=(-34.25,-11,-59.5343) rot=(0,0,1;0rad)
  Height = 56.2843
  Length = 9
  MapMode = 5
  Placement = pos=(-34.25,-11,-59.5343) rot=(0,0,1;0rad)
  Support = -> [XY_Plane081]
  Width = 22
  expr: .AttachmentOffset.Base.x = -<<Common>>#<<Parameters>>.sec_mdia / 2 - 3
  expr: .AttachmentOffset.Base.y = -<<Common>>#<<Parameters>>.sec_collbolt * 5.5 / 2
  expr: .AttachmentOffset.Base.z = -<<Common>>#<<Parameters>>.sec_mdia / 2 - <<Common>>#<<Parameters>>.sec_mfloat * sqrt(2) - <<Common>>#<<Parameters>>.sec_mthick * sqrt(2) - <<Common>>#<<Parameters>>.sec_fthick * 2 * sqrt(2)
  expr: Height = <<Common>>#<<Parameters>>.sec_mdia / 2 + <<Common>>#<<Parameters>>.sec_mfloat * sqrt(2) + <<Common>>#<<Parameters>>.sec_mthick * sqrt(2) + <<Common>>#<<Parameters>>.sec_fthick * 2 * sqrt(2) + <<Common>>#<<Parameters>>.sec_sidebolt * 3 - (<<Common>>#<<Parameters>>.sec_hubdia * 0.75 + 0.5) / 2
  expr: Length = <<Common>>#<<Parameters>>.sec_fthick * 3
  expr: Width = <<Common>>#<<Parameters>>.sec_collbolt * 5.5
FEATURE [Sketcher::SketchObject] Sketch136  label="SecondaryClip_Profile_Sketch"
  FullyConstrained = true
  MapMode = 5
  Placement = pos=(0,0,0) rot=(0.57735,0.57735,0.57735;2.0944rad)
  Support = -> [YZ_Plane081]
  expr: Constraints[15] = (<<Common>>#<<Parameters>>.sec_hubdia * 0.75 + 0.5) / 2
  expr: Constraints[7] = <<Common>>#<<Parameters>>.sec_collbolt * 1.1
  expr: Constraints[8] = <<Common>>#<<Parameters>>.sec_mtvar
  sketch-geometry (7):
    g0: ArcOfCircle CenterX=0 CenterY=-13.25 CenterZ=0 NormalX=0 NormalY=0 NormalZ=1 AngleXU=0 Radius=2.2 StartAngle=4e-16 EndAngle=3.14159
    g1: ArcOfCircle CenterX=-1e-16 CenterY=-17.25 CenterZ=0 NormalX=0 NormalY=0 NormalZ=1 AngleXU=0 Radius=2.2 StartAngle=3.14159 EndAngle=6.28319
    g2: LineSegment StartX=-2.2 StartY=-13.25 StartZ=0 EndX=-2.2 EndY=-17.25 EndZ=0
    g3: LineSegment StartX=2.2 StartY=-13.25 StartZ=0 EndX=2.2 EndY=-17.25 EndZ=0
    g4: GeomPoint X=0 Y=-15.25 Z=0
    g5: LineSegment StartX=0 StartY=-13.25 StartZ=0 EndX=0 EndY=-15.25 EndZ=0
    g6: LineSegment StartX=0 StartY=-15.25 StartZ=0 EndX=-1e-16 EndY=-17.25 EndZ=0
  constraints (16):
    c: Tangent(g0,g3) = 1.5708
    c: Tangent(g0,g2) = -1.5708
    c: Tangent(g2,g1) = -1.5708
    c: Tangent(g3,g1) = 1.5708
    c: Vertical(g2)
    c: Equal(g0,g1)
    c: PointOnObject(g0,g-2)
    c: Diameter(g0) = 4.4
    c: DistanceY(g3,g3) = 4
    c: Coincident(g5,g0)
    c: Coincident(g5,g4)
    c: Vertical(g5)
    c: Coincident(g6,g4)
    c: Coincident(g6,g1)
    c: Equal(g5,g6)
    c: DistanceY(g4,g-1) = 15.25
FEATURE [PartDesign::Pocket] Pocket077  label="SecondaryClip_Profile_Cut"
  BaseFeature = -> Box
  Direction = (-1,2e-16,-3e-16)
  Length = 5
  Length2 = 100
  Placement = pos=(-34.25,-11,-59.5343) rot=(0,0,1;0rad)
  Profile = -> Sketch136
  Type = 1
FEATURE [Sketcher::SketchObject] Sketch228  label="SecondaryClip_Inner_Sketch"
  FullyConstrained = true
  MapMode = 5
  Placement = pos=(0,0,0) rot=(1,0,0;1.5708rad)
  Support = -> [XZ_Plane081]
  expr: Constraints[10] = <<Common>>#<<Parameters>>.sec_fthick
  expr: Constraints[11] = <<Common>>#<<Parameters>>.sec_mdia / 2 + 0.7 / 2
  expr: Constraints[12] = <<Common>>#<<Parameters>>.sec_sidebolt * 3
  expr: Constraints[13] = <<Common>>#<<Parameters>>.sec_mdia / 2 + <<Common>>#<<Parameters>>.sec_mthick * sqrt(2) + <<Common>>#<<Parameters>>.sec_mfloat * sqrt(2) + 0.7
  expr: Constraints[14] = <<Common>>#<<Parameters>>.sec_sidebolt * 3
  expr: Constraints[19] = <<Common>>#<<Parameters>>.sec_fthick * sqrt(2)
  expr: Constraints[25] = <<Common>>#<<Parameters>>.sec_fthick / 2
  expr: Constraints[26] = <<Common>>#<<Parameters>>.sec_fthick
  sketch-geometry (9):
    g0: LineSegment StartX=-31.6 StartY=0 StartZ=0 EndX=-31.6 EndY=-51.749 EndZ=0
    g1: LineSegment StartX=-31.6 StartY=-51.749 StartZ=0 EndX=-28.6 EndY=-48.749 EndZ=0
    g2: LineSegment StartX=-36.1 StartY=-60.749 StartZ=0 EndX=-19.6 EndY=-60.749 EndZ=0
    g3: LineSegment StartX=-19.6 StartY=-60.749 StartZ=0 EndX=-19.6 EndY=0 EndZ=0
    g4: LineSegment StartX=-19.6 StartY=0 StartZ=0 EndX=-31.6 EndY=0 EndZ=0
    g5: LineSegment StartX=-28.6 StartY=-48.749 StartZ=0 EndX=-28.6 EndY=-52.9916 EndZ=0
    g6: LineSegment StartX=-28.6 StartY=-52.9916 StartZ=0 EndX=-33.1 EndY=-57.4916 EndZ=0
    g7: LineSegment StartX=-33.1 StartY=-57.4916 StartZ=0 EndX=-36.1 EndY=-57.4916 EndZ=0
    g8: LineSegment StartX=-36.1 StartY=-57.4916 StartZ=0 EndX=-36.1 EndY=-60.749 EndZ=0
  constraints (27):
    c: PointOnObject(g0,g-1)
    c: Vertical(g0)
    c: Coincident(g1,g0)
    c: Horizontal(g2)
    c: Coincident(g3,g2)
    c: Vertical(g3)
    c: Coincident(g4,g3)
    c: Coincident(g4,g0)
    c: PointOnObject(g3,g-1)
    c: Angle(g1,g0) = 0.785398
    c: DistanceX(g0,g1) = 3
    c: DistanceX(g0,g-1) = 31.6
    c: DistanceX(g4,g4) = 12
    c: DistanceY(g0,g0) = 51.749
    c: DistanceY(g2,g1) = 12
    c: Coincident(g5,g1)
    c: Vertical(g5)
    c: Coincident(g6,g5)
    c: Parallel(g6,g1)
    c: DistanceY(g5,g5) = 4.24264
    c: Coincident(g7,g6)
    c: Horizontal(g7)
    c: Coincident(g8,g7)
    c: Coincident(g8,g2)
    c: Vertical(g8)
    c: DistanceX(g6,g0) = 1.5
    c: DistanceX(g7,g7) = 3
FEATURE [PartDesign::Groove] Groove003  label="SecondaryClip_Inner_Groove"
  Angle = 360
  Axis = (-3e-16,3e-16,1)
  Base = (0,0,0)
  BaseFeature = -> Pocket077
  Placement = pos=(-34.25,-11,-59.5343) rot=(0,0,1;0rad)
  Profile = -> Sketch228
  ReferenceAxis = -> Z_Axis081
  Reversed = true
FEATURE [PartDesign::Fillet] Fillet010  label="SecondaryClip_Fillet"
  Base = -> Groove003 [Edge9,Edge10,Edge18,Edge19,Edge20,Edge15,Edge14]
  BaseFeature = -> Groove003
  Placement = pos=(-34.25,-11,-59.5343) rot=(0,0,1;0rad)
  Radius = 1
  SupportTransform = false
  UseAllEdges = false
  expr: Radius = <<Common>>#<<Parameters>>.sec_fillet / 2
FEATURE [PartDesign::CoordinateSystem] Local_CS304  label="LCS_SecondaryClip_Bolt"
  AttacherType = Attacher::AttachEngine3D
  AttachmentOffset = pos=(0,0,0) rot=(0,0,1;3.14159rad)
  MapMode = 45
  Placement = pos=(-31.5233,9e-16,-15.25) rot=(0,-1,0;1.5708rad)
  Support = -> [Groove003]
FEATURE [PartDesign::Chamfer] Chamfer001  label="SecondaryClip_Chamfer"
  Angle = 45
  Base = -> Fillet010 [Edge4,Edge6,Edge8,Edge7,Edge5,Edge3,Edge1,Edge2,Edge12,Edge10,Edge9,Edge11]
  BaseFeature = -> Fillet010
  ChamferType = 0
  FlipDirection = false
  Placement = pos=(-34.25,-11,-59.5343) rot=(0,0,1;0rad)
  Size = 0.4
  Size2 = 1
  SupportTransform = false
  UseAllEdges = false
FEATURE [PartDesign::Body] Body022028  label="SecondaryClip"
  Group = -> [Box,Sketch136,Pocket077,Sketch228,Groove003,Fillet010,Local_CS304,Chamfer001]
  Origin = -> Origin081
  Placement = pos=(-3.125,0,854.799) rot=(0,0,1;0rad)
  Tip = -> Chamfer001
  expr: .Placement.Base.x = -<<Common>>#<<Parameters>>.sec_offset_x
  expr: .Placement.Base.z = <<Common>>#<<Parameters>>.datum_sec_mirrorpad
